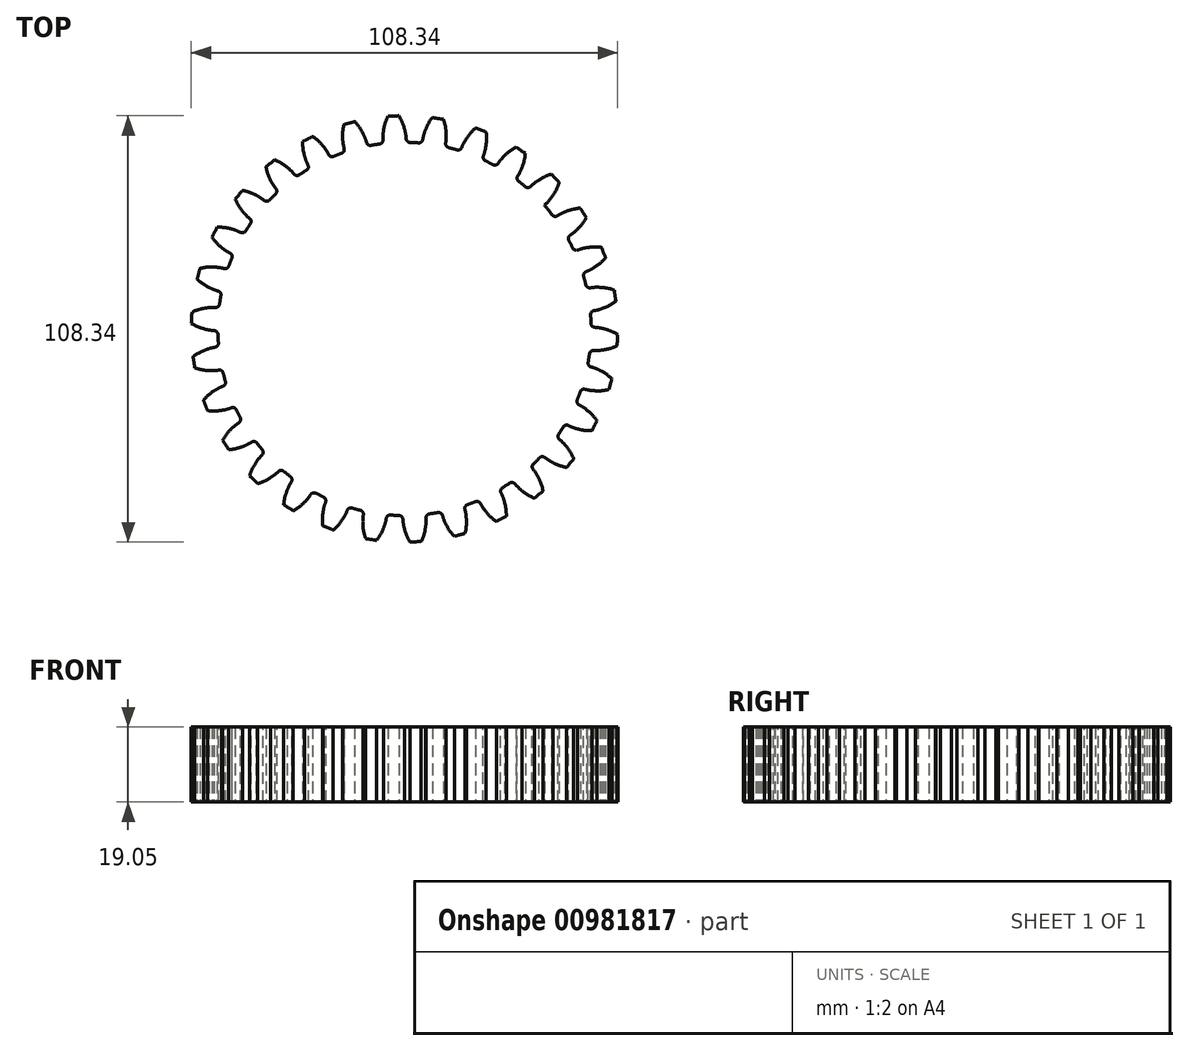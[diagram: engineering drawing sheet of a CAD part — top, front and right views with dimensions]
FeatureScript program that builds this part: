
annotation { "Feature Type Name" : "Feature", "Feature Type Description" : "" }
export const myFeature = defineFeature(function(context is Context, id is Id, definition is map)
    precondition{}
    {
        {
            var Q0;
            Q0=qCreatedBy(makeId("Top.planeOp"),FACE);
            var sketch = newSketch(context, id + "F0", { "sketchPlane" : qUnion([Q0])});
            skCircle(sketch, "E0", {"center": v(0, 0) * mm, "radius": 47.4 * mm});
            skCircle(sketch, "E1", {"center": v(0, 0) * mm, "radius": 50.8 * mm, "construction": true});
            skCircle(sketch, "E2", {"center": v(0, 0) * mm, "radius": 54.2 * mm, "construction": true});
            skLineSegment(sketch, "E3", {"start": v(0, 0) * mm, "end": v(0, 78.4) * mm, "construction": true});
            skLineSegment(sketch, "E4", {"start": v(0, 0) * mm, "end": v(-4.02, 76.64) * mm, "construction": true});
            skLineSegment(sketch, "E5", {"start": v(0, 50.8) * mm, "end": v(-70.01, 50.8) * mm, "construction": true});
            skLineSegment(sketch, "E6", {"start": v(0, 50.8) * mm, "end": v(-69.63, 32.8) * mm, "construction": true});
            skCircle(sketch, "E7", {"center": v(0, 0) * mm, "radius": 49.18 * mm, "construction": true});
            skCircle(sketch, "E8", {"center": v(0, 50.8) * mm, "radius": 12.7 * mm, "construction": true});
            skCircle(sketch, "E9", {"center": v(-12.29, 47.6) * mm, "radius": 12.7 * mm, "construction": true});
            skArc(sketch, "E10", {"start": v(0, 50.8) * mm, "mid": v(-0.57, 52.54) * mm, "end": v(-1.42, 54.17) * mm});
            skArc(sketch, "E11", {"start": v(0.4, 47.4) * mm, "mid": v(0.35, 49.12) * mm, "end": v(0, 50.8) * mm});
            skArc(sketch, "E12.MirrorCS", {"start": v(-5.36, 47.1) * mm, "mid": v(-5.48, 48.82) * mm, "end": v(-5.31, 50.52) * mm});
            skArc(sketch, "E13.MirrorCS", {"start": v(-5.31, 50.52) * mm, "mid": v(-4.92, 52.32) * mm, "end": v(-4.25, 54.02) * mm});
            skArc(sketch, "E14", {"start": v(-4.25, 54.02) * mm, "mid": v(-2.83, 54.07) * mm, "end": v(-1.42, 54.17) * mm});
            skSolve(sketch);
        }
        {
            var Q0;
            {var subQ0=sQuery(id+"F0.wireOp",EDGE,"E0");var subQ1=makeQuery(id+"F0.imprint","INTERSECT",VERTEX,{"derivedFrom":[subQ0,sQuery(id+"F0.wireOp",EDGE,"E11")]});Q0=makeQuery(id+"F0.imprint","IMPRINT",FACE,{"disambiguationData":[TD([[makeQuery(id+"F0.imprint","IMPRINT",EDGE,{"disambiguationData":[TD([[subQ1,-1.0]])],"derivedFrom":subQ0}),1.0]])]});}
            var Q1;
            Q1=makeQuery(id+"F0.imprint","IMPRINT",FACE,{"disambiguationData":[TD([[makeQuery(id+"F0.imprint","IMPRINT",EDGE,{"derivedFrom":sQuery(id+"F0.wireOp",EDGE,"E10")}),1.0]])]});
            extrude(context, id + "F1", {"entities" : qUnion([Q0, Q1]), "depth" : 19.05 * mm, "offsetDistance" : 25.4 * mm});
        }
        {
            var Q0;
            Q0=makeQuery(id+"F1.opExtrude","SWEPT_BODY",BODY,{"disambiguationData":[OSD([sQuery(id+"F0.wireOp",EDGE,"E0"),sQuery(id+"F0.wireOp",EDGE,"E10"),sQuery(id+"F0.wireOp",EDGE,"E11"),sQuery(id+"F0.wireOp",EDGE,"E12.MirrorCS"),sQuery(id+"F0.wireOp",EDGE,"E13.MirrorCS"),sQuery(id+"F0.wireOp",EDGE,"E14")])]});
            var Q1;
            Q1=makeQuery(id+"F1.opExtrude","SWEPT_FACE",FACE,{"disambiguationData":[OSD([sQuery(id+"F0.wireOp",EDGE,"E0")])]});
            circularPattern(context, id + "F2", {"entities" : qUnion([Q0]), "axis" : qUnion([Q1]), "angle" : 360 * degree, "instanceCount" : 30, "equalSpace" : true});
        }
        {
            var Q0;
            Q0=makeQuery(id+"F1.opExtrude","SWEPT_BODY",BODY,{"disambiguationData":[OSD([sQuery(id+"F0.wireOp",EDGE,"E0"),sQuery(id+"F0.wireOp",EDGE,"E10"),sQuery(id+"F0.wireOp",EDGE,"E11"),sQuery(id+"F0.wireOp",EDGE,"E12.MirrorCS"),sQuery(id+"F0.wireOp",EDGE,"E13.MirrorCS"),sQuery(id+"F0.wireOp",EDGE,"E14")])]});
            var Q1;
            Q1=makeQuery(id+"F2.opPattern","COPY",BODY,{"derivedFrom":makeQuery(id+"F1.opExtrude","SWEPT_BODY",BODY,{"disambiguationData":[OSD([sQuery(id+"F0.wireOp",EDGE,"E0"),sQuery(id+"F0.wireOp",EDGE,"E10"),sQuery(id+"F0.wireOp",EDGE,"E11"),sQuery(id+"F0.wireOp",EDGE,"E12.MirrorCS"),sQuery(id+"F0.wireOp",EDGE,"E13.MirrorCS"),sQuery(id+"F0.wireOp",EDGE,"E14")])]}),"instanceName":"1"});
            var Q2;
            Q2=makeQuery(id+"F2.opPattern","COPY",BODY,{"derivedFrom":makeQuery(id+"F1.opExtrude","SWEPT_BODY",BODY,{"disambiguationData":[OSD([sQuery(id+"F0.wireOp",EDGE,"E0"),sQuery(id+"F0.wireOp",EDGE,"E10"),sQuery(id+"F0.wireOp",EDGE,"E11"),sQuery(id+"F0.wireOp",EDGE,"E12.MirrorCS"),sQuery(id+"F0.wireOp",EDGE,"E13.MirrorCS"),sQuery(id+"F0.wireOp",EDGE,"E14")])]}),"instanceName":"2"});
            var Q3;
            Q3=makeQuery(id+"F2.opPattern","COPY",BODY,{"derivedFrom":makeQuery(id+"F1.opExtrude","SWEPT_BODY",BODY,{"disambiguationData":[OSD([sQuery(id+"F0.wireOp",EDGE,"E0"),sQuery(id+"F0.wireOp",EDGE,"E10"),sQuery(id+"F0.wireOp",EDGE,"E11"),sQuery(id+"F0.wireOp",EDGE,"E12.MirrorCS"),sQuery(id+"F0.wireOp",EDGE,"E13.MirrorCS"),sQuery(id+"F0.wireOp",EDGE,"E14")])]}),"instanceName":"4"});
            var Q4;
            Q4=makeQuery(id+"F2.opPattern","COPY",BODY,{"derivedFrom":makeQuery(id+"F1.opExtrude","SWEPT_BODY",BODY,{"disambiguationData":[OSD([sQuery(id+"F0.wireOp",EDGE,"E0"),sQuery(id+"F0.wireOp",EDGE,"E10"),sQuery(id+"F0.wireOp",EDGE,"E11"),sQuery(id+"F0.wireOp",EDGE,"E12.MirrorCS"),sQuery(id+"F0.wireOp",EDGE,"E13.MirrorCS"),sQuery(id+"F0.wireOp",EDGE,"E14")])]}),"instanceName":"3"});
            var Q5;
            Q5=makeQuery(id+"F2.opPattern","COPY",BODY,{"derivedFrom":makeQuery(id+"F1.opExtrude","SWEPT_BODY",BODY,{"disambiguationData":[OSD([sQuery(id+"F0.wireOp",EDGE,"E0"),sQuery(id+"F0.wireOp",EDGE,"E10"),sQuery(id+"F0.wireOp",EDGE,"E11"),sQuery(id+"F0.wireOp",EDGE,"E12.MirrorCS"),sQuery(id+"F0.wireOp",EDGE,"E13.MirrorCS"),sQuery(id+"F0.wireOp",EDGE,"E14")])]}),"instanceName":"6"});
            var Q6;
            Q6=makeQuery(id+"F2.opPattern","COPY",BODY,{"derivedFrom":makeQuery(id+"F1.opExtrude","SWEPT_BODY",BODY,{"disambiguationData":[OSD([sQuery(id+"F0.wireOp",EDGE,"E0"),sQuery(id+"F0.wireOp",EDGE,"E10"),sQuery(id+"F0.wireOp",EDGE,"E11"),sQuery(id+"F0.wireOp",EDGE,"E12.MirrorCS"),sQuery(id+"F0.wireOp",EDGE,"E13.MirrorCS"),sQuery(id+"F0.wireOp",EDGE,"E14")])]}),"instanceName":"5"});
            var Q7;
            Q7=makeQuery(id+"F2.opPattern","COPY",BODY,{"derivedFrom":makeQuery(id+"F1.opExtrude","SWEPT_BODY",BODY,{"disambiguationData":[OSD([sQuery(id+"F0.wireOp",EDGE,"E0"),sQuery(id+"F0.wireOp",EDGE,"E10"),sQuery(id+"F0.wireOp",EDGE,"E11"),sQuery(id+"F0.wireOp",EDGE,"E12.MirrorCS"),sQuery(id+"F0.wireOp",EDGE,"E13.MirrorCS"),sQuery(id+"F0.wireOp",EDGE,"E14")])]}),"instanceName":"7"});
            var Q8;
            Q8=makeQuery(id+"F2.opPattern","COPY",BODY,{"derivedFrom":makeQuery(id+"F1.opExtrude","SWEPT_BODY",BODY,{"disambiguationData":[OSD([sQuery(id+"F0.wireOp",EDGE,"E0"),sQuery(id+"F0.wireOp",EDGE,"E10"),sQuery(id+"F0.wireOp",EDGE,"E11"),sQuery(id+"F0.wireOp",EDGE,"E12.MirrorCS"),sQuery(id+"F0.wireOp",EDGE,"E13.MirrorCS"),sQuery(id+"F0.wireOp",EDGE,"E14")])]}),"instanceName":"8"});
            var Q9;
            Q9=makeQuery(id+"F2.opPattern","COPY",BODY,{"derivedFrom":makeQuery(id+"F1.opExtrude","SWEPT_BODY",BODY,{"disambiguationData":[OSD([sQuery(id+"F0.wireOp",EDGE,"E0"),sQuery(id+"F0.wireOp",EDGE,"E10"),sQuery(id+"F0.wireOp",EDGE,"E11"),sQuery(id+"F0.wireOp",EDGE,"E12.MirrorCS"),sQuery(id+"F0.wireOp",EDGE,"E13.MirrorCS"),sQuery(id+"F0.wireOp",EDGE,"E14")])]}),"instanceName":"9"});
            var Q10;
            Q10=makeQuery(id+"F2.opPattern","COPY",BODY,{"derivedFrom":makeQuery(id+"F1.opExtrude","SWEPT_BODY",BODY,{"disambiguationData":[OSD([sQuery(id+"F0.wireOp",EDGE,"E0"),sQuery(id+"F0.wireOp",EDGE,"E10"),sQuery(id+"F0.wireOp",EDGE,"E11"),sQuery(id+"F0.wireOp",EDGE,"E12.MirrorCS"),sQuery(id+"F0.wireOp",EDGE,"E13.MirrorCS"),sQuery(id+"F0.wireOp",EDGE,"E14")])]}),"instanceName":"10"});
            var Q11;
            Q11=makeQuery(id+"F2.opPattern","COPY",BODY,{"derivedFrom":makeQuery(id+"F1.opExtrude","SWEPT_BODY",BODY,{"disambiguationData":[OSD([sQuery(id+"F0.wireOp",EDGE,"E0"),sQuery(id+"F0.wireOp",EDGE,"E10"),sQuery(id+"F0.wireOp",EDGE,"E11"),sQuery(id+"F0.wireOp",EDGE,"E12.MirrorCS"),sQuery(id+"F0.wireOp",EDGE,"E13.MirrorCS"),sQuery(id+"F0.wireOp",EDGE,"E14")])]}),"instanceName":"11"});
            var Q12;
            Q12=makeQuery(id+"F2.opPattern","COPY",BODY,{"derivedFrom":makeQuery(id+"F1.opExtrude","SWEPT_BODY",BODY,{"disambiguationData":[OSD([sQuery(id+"F0.wireOp",EDGE,"E0"),sQuery(id+"F0.wireOp",EDGE,"E10"),sQuery(id+"F0.wireOp",EDGE,"E11"),sQuery(id+"F0.wireOp",EDGE,"E12.MirrorCS"),sQuery(id+"F0.wireOp",EDGE,"E13.MirrorCS"),sQuery(id+"F0.wireOp",EDGE,"E14")])]}),"instanceName":"12"});
            var Q13;
            Q13=makeQuery(id+"F2.opPattern","COPY",BODY,{"derivedFrom":makeQuery(id+"F1.opExtrude","SWEPT_BODY",BODY,{"disambiguationData":[OSD([sQuery(id+"F0.wireOp",EDGE,"E0"),sQuery(id+"F0.wireOp",EDGE,"E10"),sQuery(id+"F0.wireOp",EDGE,"E11"),sQuery(id+"F0.wireOp",EDGE,"E12.MirrorCS"),sQuery(id+"F0.wireOp",EDGE,"E13.MirrorCS"),sQuery(id+"F0.wireOp",EDGE,"E14")])]}),"instanceName":"13"});
            var Q14;
            Q14=makeQuery(id+"F2.opPattern","COPY",BODY,{"derivedFrom":makeQuery(id+"F1.opExtrude","SWEPT_BODY",BODY,{"disambiguationData":[OSD([sQuery(id+"F0.wireOp",EDGE,"E0"),sQuery(id+"F0.wireOp",EDGE,"E10"),sQuery(id+"F0.wireOp",EDGE,"E11"),sQuery(id+"F0.wireOp",EDGE,"E12.MirrorCS"),sQuery(id+"F0.wireOp",EDGE,"E13.MirrorCS"),sQuery(id+"F0.wireOp",EDGE,"E14")])]}),"instanceName":"14"});
            var Q15;
            Q15=makeQuery(id+"F2.opPattern","COPY",BODY,{"derivedFrom":makeQuery(id+"F1.opExtrude","SWEPT_BODY",BODY,{"disambiguationData":[OSD([sQuery(id+"F0.wireOp",EDGE,"E0"),sQuery(id+"F0.wireOp",EDGE,"E10"),sQuery(id+"F0.wireOp",EDGE,"E11"),sQuery(id+"F0.wireOp",EDGE,"E12.MirrorCS"),sQuery(id+"F0.wireOp",EDGE,"E13.MirrorCS"),sQuery(id+"F0.wireOp",EDGE,"E14")])]}),"instanceName":"16"});
            var Q16;
            Q16=makeQuery(id+"F2.opPattern","COPY",BODY,{"derivedFrom":makeQuery(id+"F1.opExtrude","SWEPT_BODY",BODY,{"disambiguationData":[OSD([sQuery(id+"F0.wireOp",EDGE,"E0"),sQuery(id+"F0.wireOp",EDGE,"E10"),sQuery(id+"F0.wireOp",EDGE,"E11"),sQuery(id+"F0.wireOp",EDGE,"E12.MirrorCS"),sQuery(id+"F0.wireOp",EDGE,"E13.MirrorCS"),sQuery(id+"F0.wireOp",EDGE,"E14")])]}),"instanceName":"17"});
            var Q17;
            Q17=makeQuery(id+"F2.opPattern","COPY",BODY,{"derivedFrom":makeQuery(id+"F1.opExtrude","SWEPT_BODY",BODY,{"disambiguationData":[OSD([sQuery(id+"F0.wireOp",EDGE,"E0"),sQuery(id+"F0.wireOp",EDGE,"E10"),sQuery(id+"F0.wireOp",EDGE,"E11"),sQuery(id+"F0.wireOp",EDGE,"E12.MirrorCS"),sQuery(id+"F0.wireOp",EDGE,"E13.MirrorCS"),sQuery(id+"F0.wireOp",EDGE,"E14")])]}),"instanceName":"15"});
            var Q18;
            Q18=makeQuery(id+"F2.opPattern","COPY",BODY,{"derivedFrom":makeQuery(id+"F1.opExtrude","SWEPT_BODY",BODY,{"disambiguationData":[OSD([sQuery(id+"F0.wireOp",EDGE,"E0"),sQuery(id+"F0.wireOp",EDGE,"E10"),sQuery(id+"F0.wireOp",EDGE,"E11"),sQuery(id+"F0.wireOp",EDGE,"E12.MirrorCS"),sQuery(id+"F0.wireOp",EDGE,"E13.MirrorCS"),sQuery(id+"F0.wireOp",EDGE,"E14")])]}),"instanceName":"18"});
            var Q19;
            Q19=makeQuery(id+"F2.opPattern","COPY",BODY,{"derivedFrom":makeQuery(id+"F1.opExtrude","SWEPT_BODY",BODY,{"disambiguationData":[OSD([sQuery(id+"F0.wireOp",EDGE,"E0"),sQuery(id+"F0.wireOp",EDGE,"E10"),sQuery(id+"F0.wireOp",EDGE,"E11"),sQuery(id+"F0.wireOp",EDGE,"E12.MirrorCS"),sQuery(id+"F0.wireOp",EDGE,"E13.MirrorCS"),sQuery(id+"F0.wireOp",EDGE,"E14")])]}),"instanceName":"19"});
            var Q20;
            Q20=makeQuery(id+"F2.opPattern","COPY",BODY,{"derivedFrom":makeQuery(id+"F1.opExtrude","SWEPT_BODY",BODY,{"disambiguationData":[OSD([sQuery(id+"F0.wireOp",EDGE,"E0"),sQuery(id+"F0.wireOp",EDGE,"E10"),sQuery(id+"F0.wireOp",EDGE,"E11"),sQuery(id+"F0.wireOp",EDGE,"E12.MirrorCS"),sQuery(id+"F0.wireOp",EDGE,"E13.MirrorCS"),sQuery(id+"F0.wireOp",EDGE,"E14")])]}),"instanceName":"20"});
            var Q21;
            Q21=makeQuery(id+"F2.opPattern","COPY",BODY,{"derivedFrom":makeQuery(id+"F1.opExtrude","SWEPT_BODY",BODY,{"disambiguationData":[OSD([sQuery(id+"F0.wireOp",EDGE,"E0"),sQuery(id+"F0.wireOp",EDGE,"E10"),sQuery(id+"F0.wireOp",EDGE,"E11"),sQuery(id+"F0.wireOp",EDGE,"E12.MirrorCS"),sQuery(id+"F0.wireOp",EDGE,"E13.MirrorCS"),sQuery(id+"F0.wireOp",EDGE,"E14")])]}),"instanceName":"21"});
            var Q22;
            Q22=makeQuery(id+"F2.opPattern","COPY",BODY,{"derivedFrom":makeQuery(id+"F1.opExtrude","SWEPT_BODY",BODY,{"disambiguationData":[OSD([sQuery(id+"F0.wireOp",EDGE,"E0"),sQuery(id+"F0.wireOp",EDGE,"E10"),sQuery(id+"F0.wireOp",EDGE,"E11"),sQuery(id+"F0.wireOp",EDGE,"E12.MirrorCS"),sQuery(id+"F0.wireOp",EDGE,"E13.MirrorCS"),sQuery(id+"F0.wireOp",EDGE,"E14")])]}),"instanceName":"22"});
            var Q23;
            Q23=makeQuery(id+"F2.opPattern","COPY",BODY,{"derivedFrom":makeQuery(id+"F1.opExtrude","SWEPT_BODY",BODY,{"disambiguationData":[OSD([sQuery(id+"F0.wireOp",EDGE,"E0"),sQuery(id+"F0.wireOp",EDGE,"E10"),sQuery(id+"F0.wireOp",EDGE,"E11"),sQuery(id+"F0.wireOp",EDGE,"E12.MirrorCS"),sQuery(id+"F0.wireOp",EDGE,"E13.MirrorCS"),sQuery(id+"F0.wireOp",EDGE,"E14")])]}),"instanceName":"23"});
            var Q24;
            Q24=makeQuery(id+"F2.opPattern","COPY",BODY,{"derivedFrom":makeQuery(id+"F1.opExtrude","SWEPT_BODY",BODY,{"disambiguationData":[OSD([sQuery(id+"F0.wireOp",EDGE,"E0"),sQuery(id+"F0.wireOp",EDGE,"E10"),sQuery(id+"F0.wireOp",EDGE,"E11"),sQuery(id+"F0.wireOp",EDGE,"E12.MirrorCS"),sQuery(id+"F0.wireOp",EDGE,"E13.MirrorCS"),sQuery(id+"F0.wireOp",EDGE,"E14")])]}),"instanceName":"24"});
            var Q25;
            Q25=makeQuery(id+"F2.opPattern","COPY",BODY,{"derivedFrom":makeQuery(id+"F1.opExtrude","SWEPT_BODY",BODY,{"disambiguationData":[OSD([sQuery(id+"F0.wireOp",EDGE,"E0"),sQuery(id+"F0.wireOp",EDGE,"E10"),sQuery(id+"F0.wireOp",EDGE,"E11"),sQuery(id+"F0.wireOp",EDGE,"E12.MirrorCS"),sQuery(id+"F0.wireOp",EDGE,"E13.MirrorCS"),sQuery(id+"F0.wireOp",EDGE,"E14")])]}),"instanceName":"25"});
            var Q26;
            Q26=makeQuery(id+"F2.opPattern","COPY",BODY,{"derivedFrom":makeQuery(id+"F1.opExtrude","SWEPT_BODY",BODY,{"disambiguationData":[OSD([sQuery(id+"F0.wireOp",EDGE,"E0"),sQuery(id+"F0.wireOp",EDGE,"E10"),sQuery(id+"F0.wireOp",EDGE,"E11"),sQuery(id+"F0.wireOp",EDGE,"E12.MirrorCS"),sQuery(id+"F0.wireOp",EDGE,"E13.MirrorCS"),sQuery(id+"F0.wireOp",EDGE,"E14")])]}),"instanceName":"26"});
            var Q27;
            Q27=makeQuery(id+"F2.opPattern","COPY",BODY,{"derivedFrom":makeQuery(id+"F1.opExtrude","SWEPT_BODY",BODY,{"disambiguationData":[OSD([sQuery(id+"F0.wireOp",EDGE,"E0"),sQuery(id+"F0.wireOp",EDGE,"E10"),sQuery(id+"F0.wireOp",EDGE,"E11"),sQuery(id+"F0.wireOp",EDGE,"E12.MirrorCS"),sQuery(id+"F0.wireOp",EDGE,"E13.MirrorCS"),sQuery(id+"F0.wireOp",EDGE,"E14")])]}),"instanceName":"27"});
            var Q28;
            Q28=makeQuery(id+"F2.opPattern","COPY",BODY,{"derivedFrom":makeQuery(id+"F1.opExtrude","SWEPT_BODY",BODY,{"disambiguationData":[OSD([sQuery(id+"F0.wireOp",EDGE,"E0"),sQuery(id+"F0.wireOp",EDGE,"E10"),sQuery(id+"F0.wireOp",EDGE,"E11"),sQuery(id+"F0.wireOp",EDGE,"E12.MirrorCS"),sQuery(id+"F0.wireOp",EDGE,"E13.MirrorCS"),sQuery(id+"F0.wireOp",EDGE,"E14")])]}),"instanceName":"28"});
            var Q29;
            Q29=makeQuery(id+"F2.opPattern","COPY",BODY,{"derivedFrom":makeQuery(id+"F1.opExtrude","SWEPT_BODY",BODY,{"disambiguationData":[OSD([sQuery(id+"F0.wireOp",EDGE,"E0"),sQuery(id+"F0.wireOp",EDGE,"E10"),sQuery(id+"F0.wireOp",EDGE,"E11"),sQuery(id+"F0.wireOp",EDGE,"E12.MirrorCS"),sQuery(id+"F0.wireOp",EDGE,"E13.MirrorCS"),sQuery(id+"F0.wireOp",EDGE,"E14")])]}),"instanceName":"29"});
            booleanBodies(context, id + "F3", {"operationType" : BooleanOperationType.UNION, "tools" : qUnion([Q0, Q1, Q2, Q3, Q4, Q5, Q6, Q7, Q8, Q9, Q10, Q11, Q12, Q13, Q14, Q15, Q16, Q17, Q18, Q19, Q20, Q21, Q22, Q23, Q24, Q25, Q26, Q27, Q28, Q29])});
        }
        {
            var Q0;
            {var subQ0=makeQuery(id+"F1.opExtrude","SWEPT_FACE",FACE,{"disambiguationData":[OSD([sQuery(id+"F0.wireOp",EDGE,"E0")])]});Q0=makeQuery(id+"F3.opBoolean","INTERSECT",EDGE,{"disambiguationData":[topologyDisambiguationEdgeConnected([makeQuery(id+"F2.opPattern","COPY",FACE,{"derivedFrom":makeQuery(id+"F1.opExtrude","SWEPT_FACE",FACE,{"disambiguationData":[OSD([sQuery(id+"F0.wireOp",EDGE,"E11")])]}),"instanceName":"21"})])],"derivedFrom":[subQ0,makeQuery(id+"F2.opPattern","COPY",FACE,{"derivedFrom":subQ0,"instanceName":"1"}),makeQuery(id+"F2.opPattern","COPY",FACE,{"derivedFrom":subQ0,"instanceName":"2"}),makeQuery(id+"F2.opPattern","COPY",FACE,{"derivedFrom":subQ0,"instanceName":"3"}),makeQuery(id+"F2.opPattern","COPY",FACE,{"derivedFrom":subQ0,"instanceName":"4"}),makeQuery(id+"F2.opPattern","COPY",FACE,{"derivedFrom":subQ0,"instanceName":"5"}),makeQuery(id+"F2.opPattern","COPY",FACE,{"derivedFrom":subQ0,"instanceName":"6"}),makeQuery(id+"F2.opPattern","COPY",FACE,{"derivedFrom":subQ0,"instanceName":"7"}),makeQuery(id+"F2.opPattern","COPY",FACE,{"derivedFrom":subQ0,"instanceName":"8"}),makeQuery(id+"F2.opPattern","COPY",FACE,{"derivedFrom":subQ0,"instanceName":"9"}),makeQuery(id+"F2.opPattern","COPY",FACE,{"derivedFrom":subQ0,"instanceName":"10"}),makeQuery(id+"F2.opPattern","COPY",FACE,{"derivedFrom":subQ0,"instanceName":"11"}),makeQuery(id+"F2.opPattern","COPY",FACE,{"derivedFrom":subQ0,"instanceName":"12"}),makeQuery(id+"F2.opPattern","COPY",FACE,{"derivedFrom":subQ0,"instanceName":"13"}),makeQuery(id+"F2.opPattern","COPY",FACE,{"derivedFrom":subQ0,"instanceName":"14"}),makeQuery(id+"F2.opPattern","COPY",FACE,{"derivedFrom":subQ0,"instanceName":"15"}),makeQuery(id+"F2.opPattern","COPY",FACE,{"derivedFrom":subQ0,"instanceName":"16"}),makeQuery(id+"F2.opPattern","COPY",FACE,{"derivedFrom":subQ0,"instanceName":"17"}),makeQuery(id+"F2.opPattern","COPY",FACE,{"derivedFrom":subQ0,"instanceName":"18"}),makeQuery(id+"F2.opPattern","COPY",FACE,{"derivedFrom":subQ0,"instanceName":"19"}),makeQuery(id+"F2.opPattern","COPY",FACE,{"derivedFrom":subQ0,"instanceName":"20"}),makeQuery(id+"F2.opPattern","COPY",FACE,{"derivedFrom":subQ0,"instanceName":"22"})]});}
            var Q1;
            {var subQ0=makeQuery(id+"F1.opExtrude","SWEPT_FACE",FACE,{"disambiguationData":[OSD([sQuery(id+"F0.wireOp",EDGE,"E0")])]});Q1=makeQuery(id+"F3.opBoolean","INTERSECT",EDGE,{"disambiguationData":[topologyDisambiguationEdgeConnected([makeQuery(id+"F2.opPattern","COPY",FACE,{"derivedFrom":makeQuery(id+"F1.opExtrude","SWEPT_FACE",FACE,{"disambiguationData":[OSD([sQuery(id+"F0.wireOp",EDGE,"E12.MirrorCS")])]}),"instanceName":"22"})])],"derivedFrom":[subQ0,makeQuery(id+"F2.opPattern","COPY",FACE,{"derivedFrom":subQ0,"instanceName":"1"}),makeQuery(id+"F2.opPattern","COPY",FACE,{"derivedFrom":subQ0,"instanceName":"2"}),makeQuery(id+"F2.opPattern","COPY",FACE,{"derivedFrom":subQ0,"instanceName":"3"}),makeQuery(id+"F2.opPattern","COPY",FACE,{"derivedFrom":subQ0,"instanceName":"4"}),makeQuery(id+"F2.opPattern","COPY",FACE,{"derivedFrom":subQ0,"instanceName":"5"}),makeQuery(id+"F2.opPattern","COPY",FACE,{"derivedFrom":subQ0,"instanceName":"6"}),makeQuery(id+"F2.opPattern","COPY",FACE,{"derivedFrom":subQ0,"instanceName":"7"}),makeQuery(id+"F2.opPattern","COPY",FACE,{"derivedFrom":subQ0,"instanceName":"8"}),makeQuery(id+"F2.opPattern","COPY",FACE,{"derivedFrom":subQ0,"instanceName":"9"}),makeQuery(id+"F2.opPattern","COPY",FACE,{"derivedFrom":subQ0,"instanceName":"10"}),makeQuery(id+"F2.opPattern","COPY",FACE,{"derivedFrom":subQ0,"instanceName":"11"}),makeQuery(id+"F2.opPattern","COPY",FACE,{"derivedFrom":subQ0,"instanceName":"12"}),makeQuery(id+"F2.opPattern","COPY",FACE,{"derivedFrom":subQ0,"instanceName":"13"}),makeQuery(id+"F2.opPattern","COPY",FACE,{"derivedFrom":subQ0,"instanceName":"14"}),makeQuery(id+"F2.opPattern","COPY",FACE,{"derivedFrom":subQ0,"instanceName":"15"}),makeQuery(id+"F2.opPattern","COPY",FACE,{"derivedFrom":subQ0,"instanceName":"16"}),makeQuery(id+"F2.opPattern","COPY",FACE,{"derivedFrom":subQ0,"instanceName":"17"}),makeQuery(id+"F2.opPattern","COPY",FACE,{"derivedFrom":subQ0,"instanceName":"18"}),makeQuery(id+"F2.opPattern","COPY",FACE,{"derivedFrom":subQ0,"instanceName":"19"}),makeQuery(id+"F2.opPattern","COPY",FACE,{"derivedFrom":subQ0,"instanceName":"20"}),makeQuery(id+"F2.opPattern","COPY",FACE,{"derivedFrom":subQ0,"instanceName":"21"}),makeQuery(id+"F2.opPattern","COPY",FACE,{"derivedFrom":subQ0,"instanceName":"23"})]});}
            var Q2;
            {var subQ0=makeQuery(id+"F1.opExtrude","SWEPT_FACE",FACE,{"disambiguationData":[OSD([sQuery(id+"F0.wireOp",EDGE,"E0")])]});Q2=makeQuery(id+"F3.opBoolean","INTERSECT",EDGE,{"disambiguationData":[topologyDisambiguationEdgeConnected([makeQuery(id+"F2.opPattern","COPY",FACE,{"derivedFrom":makeQuery(id+"F1.opExtrude","SWEPT_FACE",FACE,{"disambiguationData":[OSD([sQuery(id+"F0.wireOp",EDGE,"E11")])]}),"instanceName":"22"})])],"derivedFrom":[subQ0,makeQuery(id+"F2.opPattern","COPY",FACE,{"derivedFrom":subQ0,"instanceName":"1"}),makeQuery(id+"F2.opPattern","COPY",FACE,{"derivedFrom":subQ0,"instanceName":"2"}),makeQuery(id+"F2.opPattern","COPY",FACE,{"derivedFrom":subQ0,"instanceName":"3"}),makeQuery(id+"F2.opPattern","COPY",FACE,{"derivedFrom":subQ0,"instanceName":"4"}),makeQuery(id+"F2.opPattern","COPY",FACE,{"derivedFrom":subQ0,"instanceName":"5"}),makeQuery(id+"F2.opPattern","COPY",FACE,{"derivedFrom":subQ0,"instanceName":"6"}),makeQuery(id+"F2.opPattern","COPY",FACE,{"derivedFrom":subQ0,"instanceName":"7"}),makeQuery(id+"F2.opPattern","COPY",FACE,{"derivedFrom":subQ0,"instanceName":"8"}),makeQuery(id+"F2.opPattern","COPY",FACE,{"derivedFrom":subQ0,"instanceName":"9"}),makeQuery(id+"F2.opPattern","COPY",FACE,{"derivedFrom":subQ0,"instanceName":"10"}),makeQuery(id+"F2.opPattern","COPY",FACE,{"derivedFrom":subQ0,"instanceName":"11"}),makeQuery(id+"F2.opPattern","COPY",FACE,{"derivedFrom":subQ0,"instanceName":"12"}),makeQuery(id+"F2.opPattern","COPY",FACE,{"derivedFrom":subQ0,"instanceName":"13"}),makeQuery(id+"F2.opPattern","COPY",FACE,{"derivedFrom":subQ0,"instanceName":"14"}),makeQuery(id+"F2.opPattern","COPY",FACE,{"derivedFrom":subQ0,"instanceName":"15"}),makeQuery(id+"F2.opPattern","COPY",FACE,{"derivedFrom":subQ0,"instanceName":"16"}),makeQuery(id+"F2.opPattern","COPY",FACE,{"derivedFrom":subQ0,"instanceName":"17"}),makeQuery(id+"F2.opPattern","COPY",FACE,{"derivedFrom":subQ0,"instanceName":"18"}),makeQuery(id+"F2.opPattern","COPY",FACE,{"derivedFrom":subQ0,"instanceName":"19"}),makeQuery(id+"F2.opPattern","COPY",FACE,{"derivedFrom":subQ0,"instanceName":"20"}),makeQuery(id+"F2.opPattern","COPY",FACE,{"derivedFrom":subQ0,"instanceName":"21"}),makeQuery(id+"F2.opPattern","COPY",FACE,{"derivedFrom":subQ0,"instanceName":"23"})]});}
            var Q3;
            {var subQ0=makeQuery(id+"F1.opExtrude","SWEPT_FACE",FACE,{"disambiguationData":[OSD([sQuery(id+"F0.wireOp",EDGE,"E0")])]});Q3=makeQuery(id+"F3.opBoolean","INTERSECT",EDGE,{"disambiguationData":[topologyDisambiguationEdgeConnected([makeQuery(id+"F2.opPattern","COPY",FACE,{"derivedFrom":makeQuery(id+"F1.opExtrude","SWEPT_FACE",FACE,{"disambiguationData":[OSD([sQuery(id+"F0.wireOp",EDGE,"E12.MirrorCS")])]}),"instanceName":"23"})])],"derivedFrom":[subQ0,makeQuery(id+"F2.opPattern","COPY",FACE,{"derivedFrom":subQ0,"instanceName":"1"}),makeQuery(id+"F2.opPattern","COPY",FACE,{"derivedFrom":subQ0,"instanceName":"2"}),makeQuery(id+"F2.opPattern","COPY",FACE,{"derivedFrom":subQ0,"instanceName":"3"}),makeQuery(id+"F2.opPattern","COPY",FACE,{"derivedFrom":subQ0,"instanceName":"4"}),makeQuery(id+"F2.opPattern","COPY",FACE,{"derivedFrom":subQ0,"instanceName":"5"}),makeQuery(id+"F2.opPattern","COPY",FACE,{"derivedFrom":subQ0,"instanceName":"6"}),makeQuery(id+"F2.opPattern","COPY",FACE,{"derivedFrom":subQ0,"instanceName":"7"}),makeQuery(id+"F2.opPattern","COPY",FACE,{"derivedFrom":subQ0,"instanceName":"8"}),makeQuery(id+"F2.opPattern","COPY",FACE,{"derivedFrom":subQ0,"instanceName":"9"}),makeQuery(id+"F2.opPattern","COPY",FACE,{"derivedFrom":subQ0,"instanceName":"10"}),makeQuery(id+"F2.opPattern","COPY",FACE,{"derivedFrom":subQ0,"instanceName":"11"}),makeQuery(id+"F2.opPattern","COPY",FACE,{"derivedFrom":subQ0,"instanceName":"12"}),makeQuery(id+"F2.opPattern","COPY",FACE,{"derivedFrom":subQ0,"instanceName":"13"}),makeQuery(id+"F2.opPattern","COPY",FACE,{"derivedFrom":subQ0,"instanceName":"14"}),makeQuery(id+"F2.opPattern","COPY",FACE,{"derivedFrom":subQ0,"instanceName":"15"}),makeQuery(id+"F2.opPattern","COPY",FACE,{"derivedFrom":subQ0,"instanceName":"16"}),makeQuery(id+"F2.opPattern","COPY",FACE,{"derivedFrom":subQ0,"instanceName":"17"}),makeQuery(id+"F2.opPattern","COPY",FACE,{"derivedFrom":subQ0,"instanceName":"18"}),makeQuery(id+"F2.opPattern","COPY",FACE,{"derivedFrom":subQ0,"instanceName":"19"}),makeQuery(id+"F2.opPattern","COPY",FACE,{"derivedFrom":subQ0,"instanceName":"20"}),makeQuery(id+"F2.opPattern","COPY",FACE,{"derivedFrom":subQ0,"instanceName":"21"}),makeQuery(id+"F2.opPattern","COPY",FACE,{"derivedFrom":subQ0,"instanceName":"22"}),makeQuery(id+"F2.opPattern","COPY",FACE,{"derivedFrom":subQ0,"instanceName":"24"})]});}
            var Q4;
            {var subQ0=makeQuery(id+"F1.opExtrude","SWEPT_FACE",FACE,{"disambiguationData":[OSD([sQuery(id+"F0.wireOp",EDGE,"E0")])]});Q4=makeQuery(id+"F3.opBoolean","INTERSECT",EDGE,{"disambiguationData":[topologyDisambiguationEdgeConnected([makeQuery(id+"F2.opPattern","COPY",FACE,{"derivedFrom":makeQuery(id+"F1.opExtrude","SWEPT_FACE",FACE,{"disambiguationData":[OSD([sQuery(id+"F0.wireOp",EDGE,"E11")])]}),"instanceName":"23"})])],"derivedFrom":[subQ0,makeQuery(id+"F2.opPattern","COPY",FACE,{"derivedFrom":subQ0,"instanceName":"1"}),makeQuery(id+"F2.opPattern","COPY",FACE,{"derivedFrom":subQ0,"instanceName":"2"}),makeQuery(id+"F2.opPattern","COPY",FACE,{"derivedFrom":subQ0,"instanceName":"3"}),makeQuery(id+"F2.opPattern","COPY",FACE,{"derivedFrom":subQ0,"instanceName":"4"}),makeQuery(id+"F2.opPattern","COPY",FACE,{"derivedFrom":subQ0,"instanceName":"5"}),makeQuery(id+"F2.opPattern","COPY",FACE,{"derivedFrom":subQ0,"instanceName":"6"}),makeQuery(id+"F2.opPattern","COPY",FACE,{"derivedFrom":subQ0,"instanceName":"7"}),makeQuery(id+"F2.opPattern","COPY",FACE,{"derivedFrom":subQ0,"instanceName":"8"}),makeQuery(id+"F2.opPattern","COPY",FACE,{"derivedFrom":subQ0,"instanceName":"9"}),makeQuery(id+"F2.opPattern","COPY",FACE,{"derivedFrom":subQ0,"instanceName":"10"}),makeQuery(id+"F2.opPattern","COPY",FACE,{"derivedFrom":subQ0,"instanceName":"11"}),makeQuery(id+"F2.opPattern","COPY",FACE,{"derivedFrom":subQ0,"instanceName":"12"}),makeQuery(id+"F2.opPattern","COPY",FACE,{"derivedFrom":subQ0,"instanceName":"13"}),makeQuery(id+"F2.opPattern","COPY",FACE,{"derivedFrom":subQ0,"instanceName":"14"}),makeQuery(id+"F2.opPattern","COPY",FACE,{"derivedFrom":subQ0,"instanceName":"15"}),makeQuery(id+"F2.opPattern","COPY",FACE,{"derivedFrom":subQ0,"instanceName":"16"}),makeQuery(id+"F2.opPattern","COPY",FACE,{"derivedFrom":subQ0,"instanceName":"17"}),makeQuery(id+"F2.opPattern","COPY",FACE,{"derivedFrom":subQ0,"instanceName":"18"}),makeQuery(id+"F2.opPattern","COPY",FACE,{"derivedFrom":subQ0,"instanceName":"19"}),makeQuery(id+"F2.opPattern","COPY",FACE,{"derivedFrom":subQ0,"instanceName":"20"}),makeQuery(id+"F2.opPattern","COPY",FACE,{"derivedFrom":subQ0,"instanceName":"21"}),makeQuery(id+"F2.opPattern","COPY",FACE,{"derivedFrom":subQ0,"instanceName":"22"}),makeQuery(id+"F2.opPattern","COPY",FACE,{"derivedFrom":subQ0,"instanceName":"24"})]});}
            var Q5;
            {var subQ0=makeQuery(id+"F1.opExtrude","SWEPT_FACE",FACE,{"disambiguationData":[OSD([sQuery(id+"F0.wireOp",EDGE,"E0")])]});Q5=makeQuery(id+"F3.opBoolean","INTERSECT",EDGE,{"disambiguationData":[topologyDisambiguationEdgeConnected([makeQuery(id+"F2.opPattern","COPY",FACE,{"derivedFrom":makeQuery(id+"F1.opExtrude","SWEPT_FACE",FACE,{"disambiguationData":[OSD([sQuery(id+"F0.wireOp",EDGE,"E12.MirrorCS")])]}),"instanceName":"24"})])],"derivedFrom":[subQ0,makeQuery(id+"F2.opPattern","COPY",FACE,{"derivedFrom":subQ0,"instanceName":"1"}),makeQuery(id+"F2.opPattern","COPY",FACE,{"derivedFrom":subQ0,"instanceName":"2"}),makeQuery(id+"F2.opPattern","COPY",FACE,{"derivedFrom":subQ0,"instanceName":"3"}),makeQuery(id+"F2.opPattern","COPY",FACE,{"derivedFrom":subQ0,"instanceName":"4"}),makeQuery(id+"F2.opPattern","COPY",FACE,{"derivedFrom":subQ0,"instanceName":"5"}),makeQuery(id+"F2.opPattern","COPY",FACE,{"derivedFrom":subQ0,"instanceName":"6"}),makeQuery(id+"F2.opPattern","COPY",FACE,{"derivedFrom":subQ0,"instanceName":"7"}),makeQuery(id+"F2.opPattern","COPY",FACE,{"derivedFrom":subQ0,"instanceName":"8"}),makeQuery(id+"F2.opPattern","COPY",FACE,{"derivedFrom":subQ0,"instanceName":"9"}),makeQuery(id+"F2.opPattern","COPY",FACE,{"derivedFrom":subQ0,"instanceName":"10"}),makeQuery(id+"F2.opPattern","COPY",FACE,{"derivedFrom":subQ0,"instanceName":"11"}),makeQuery(id+"F2.opPattern","COPY",FACE,{"derivedFrom":subQ0,"instanceName":"12"}),makeQuery(id+"F2.opPattern","COPY",FACE,{"derivedFrom":subQ0,"instanceName":"13"}),makeQuery(id+"F2.opPattern","COPY",FACE,{"derivedFrom":subQ0,"instanceName":"14"}),makeQuery(id+"F2.opPattern","COPY",FACE,{"derivedFrom":subQ0,"instanceName":"15"}),makeQuery(id+"F2.opPattern","COPY",FACE,{"derivedFrom":subQ0,"instanceName":"16"}),makeQuery(id+"F2.opPattern","COPY",FACE,{"derivedFrom":subQ0,"instanceName":"17"}),makeQuery(id+"F2.opPattern","COPY",FACE,{"derivedFrom":subQ0,"instanceName":"18"}),makeQuery(id+"F2.opPattern","COPY",FACE,{"derivedFrom":subQ0,"instanceName":"19"}),makeQuery(id+"F2.opPattern","COPY",FACE,{"derivedFrom":subQ0,"instanceName":"20"}),makeQuery(id+"F2.opPattern","COPY",FACE,{"derivedFrom":subQ0,"instanceName":"21"}),makeQuery(id+"F2.opPattern","COPY",FACE,{"derivedFrom":subQ0,"instanceName":"22"}),makeQuery(id+"F2.opPattern","COPY",FACE,{"derivedFrom":subQ0,"instanceName":"23"}),makeQuery(id+"F2.opPattern","COPY",FACE,{"derivedFrom":subQ0,"instanceName":"25"})]});}
            var Q6;
            {var subQ0=makeQuery(id+"F1.opExtrude","SWEPT_FACE",FACE,{"disambiguationData":[OSD([sQuery(id+"F0.wireOp",EDGE,"E0")])]});Q6=makeQuery(id+"F3.opBoolean","INTERSECT",EDGE,{"disambiguationData":[topologyDisambiguationEdgeConnected([makeQuery(id+"F2.opPattern","COPY",FACE,{"derivedFrom":makeQuery(id+"F1.opExtrude","SWEPT_FACE",FACE,{"disambiguationData":[OSD([sQuery(id+"F0.wireOp",EDGE,"E11")])]}),"instanceName":"24"})])],"derivedFrom":[subQ0,makeQuery(id+"F2.opPattern","COPY",FACE,{"derivedFrom":subQ0,"instanceName":"1"}),makeQuery(id+"F2.opPattern","COPY",FACE,{"derivedFrom":subQ0,"instanceName":"2"}),makeQuery(id+"F2.opPattern","COPY",FACE,{"derivedFrom":subQ0,"instanceName":"3"}),makeQuery(id+"F2.opPattern","COPY",FACE,{"derivedFrom":subQ0,"instanceName":"4"}),makeQuery(id+"F2.opPattern","COPY",FACE,{"derivedFrom":subQ0,"instanceName":"5"}),makeQuery(id+"F2.opPattern","COPY",FACE,{"derivedFrom":subQ0,"instanceName":"6"}),makeQuery(id+"F2.opPattern","COPY",FACE,{"derivedFrom":subQ0,"instanceName":"7"}),makeQuery(id+"F2.opPattern","COPY",FACE,{"derivedFrom":subQ0,"instanceName":"8"}),makeQuery(id+"F2.opPattern","COPY",FACE,{"derivedFrom":subQ0,"instanceName":"9"}),makeQuery(id+"F2.opPattern","COPY",FACE,{"derivedFrom":subQ0,"instanceName":"10"}),makeQuery(id+"F2.opPattern","COPY",FACE,{"derivedFrom":subQ0,"instanceName":"11"}),makeQuery(id+"F2.opPattern","COPY",FACE,{"derivedFrom":subQ0,"instanceName":"12"}),makeQuery(id+"F2.opPattern","COPY",FACE,{"derivedFrom":subQ0,"instanceName":"13"}),makeQuery(id+"F2.opPattern","COPY",FACE,{"derivedFrom":subQ0,"instanceName":"14"}),makeQuery(id+"F2.opPattern","COPY",FACE,{"derivedFrom":subQ0,"instanceName":"15"}),makeQuery(id+"F2.opPattern","COPY",FACE,{"derivedFrom":subQ0,"instanceName":"16"}),makeQuery(id+"F2.opPattern","COPY",FACE,{"derivedFrom":subQ0,"instanceName":"17"}),makeQuery(id+"F2.opPattern","COPY",FACE,{"derivedFrom":subQ0,"instanceName":"18"}),makeQuery(id+"F2.opPattern","COPY",FACE,{"derivedFrom":subQ0,"instanceName":"19"}),makeQuery(id+"F2.opPattern","COPY",FACE,{"derivedFrom":subQ0,"instanceName":"20"}),makeQuery(id+"F2.opPattern","COPY",FACE,{"derivedFrom":subQ0,"instanceName":"21"}),makeQuery(id+"F2.opPattern","COPY",FACE,{"derivedFrom":subQ0,"instanceName":"22"}),makeQuery(id+"F2.opPattern","COPY",FACE,{"derivedFrom":subQ0,"instanceName":"23"}),makeQuery(id+"F2.opPattern","COPY",FACE,{"derivedFrom":subQ0,"instanceName":"25"})]});}
            var Q7;
            {var subQ0=makeQuery(id+"F1.opExtrude","SWEPT_FACE",FACE,{"disambiguationData":[OSD([sQuery(id+"F0.wireOp",EDGE,"E0")])]});Q7=makeQuery(id+"F3.opBoolean","INTERSECT",EDGE,{"disambiguationData":[topologyDisambiguationEdgeConnected([makeQuery(id+"F2.opPattern","COPY",FACE,{"derivedFrom":makeQuery(id+"F1.opExtrude","SWEPT_FACE",FACE,{"disambiguationData":[OSD([sQuery(id+"F0.wireOp",EDGE,"E12.MirrorCS")])]}),"instanceName":"25"})])],"derivedFrom":[subQ0,makeQuery(id+"F2.opPattern","COPY",FACE,{"derivedFrom":subQ0,"instanceName":"1"}),makeQuery(id+"F2.opPattern","COPY",FACE,{"derivedFrom":subQ0,"instanceName":"2"}),makeQuery(id+"F2.opPattern","COPY",FACE,{"derivedFrom":subQ0,"instanceName":"3"}),makeQuery(id+"F2.opPattern","COPY",FACE,{"derivedFrom":subQ0,"instanceName":"4"}),makeQuery(id+"F2.opPattern","COPY",FACE,{"derivedFrom":subQ0,"instanceName":"5"}),makeQuery(id+"F2.opPattern","COPY",FACE,{"derivedFrom":subQ0,"instanceName":"6"}),makeQuery(id+"F2.opPattern","COPY",FACE,{"derivedFrom":subQ0,"instanceName":"7"}),makeQuery(id+"F2.opPattern","COPY",FACE,{"derivedFrom":subQ0,"instanceName":"8"}),makeQuery(id+"F2.opPattern","COPY",FACE,{"derivedFrom":subQ0,"instanceName":"9"}),makeQuery(id+"F2.opPattern","COPY",FACE,{"derivedFrom":subQ0,"instanceName":"10"}),makeQuery(id+"F2.opPattern","COPY",FACE,{"derivedFrom":subQ0,"instanceName":"11"}),makeQuery(id+"F2.opPattern","COPY",FACE,{"derivedFrom":subQ0,"instanceName":"12"}),makeQuery(id+"F2.opPattern","COPY",FACE,{"derivedFrom":subQ0,"instanceName":"13"}),makeQuery(id+"F2.opPattern","COPY",FACE,{"derivedFrom":subQ0,"instanceName":"14"}),makeQuery(id+"F2.opPattern","COPY",FACE,{"derivedFrom":subQ0,"instanceName":"15"}),makeQuery(id+"F2.opPattern","COPY",FACE,{"derivedFrom":subQ0,"instanceName":"16"}),makeQuery(id+"F2.opPattern","COPY",FACE,{"derivedFrom":subQ0,"instanceName":"17"}),makeQuery(id+"F2.opPattern","COPY",FACE,{"derivedFrom":subQ0,"instanceName":"18"}),makeQuery(id+"F2.opPattern","COPY",FACE,{"derivedFrom":subQ0,"instanceName":"19"}),makeQuery(id+"F2.opPattern","COPY",FACE,{"derivedFrom":subQ0,"instanceName":"20"}),makeQuery(id+"F2.opPattern","COPY",FACE,{"derivedFrom":subQ0,"instanceName":"21"}),makeQuery(id+"F2.opPattern","COPY",FACE,{"derivedFrom":subQ0,"instanceName":"22"}),makeQuery(id+"F2.opPattern","COPY",FACE,{"derivedFrom":subQ0,"instanceName":"23"}),makeQuery(id+"F2.opPattern","COPY",FACE,{"derivedFrom":subQ0,"instanceName":"24"}),makeQuery(id+"F2.opPattern","COPY",FACE,{"derivedFrom":subQ0,"instanceName":"26"})]});}
            var Q8;
            {var subQ0=makeQuery(id+"F1.opExtrude","SWEPT_FACE",FACE,{"disambiguationData":[OSD([sQuery(id+"F0.wireOp",EDGE,"E0")])]});Q8=makeQuery(id+"F3.opBoolean","INTERSECT",EDGE,{"disambiguationData":[topologyDisambiguationEdgeConnected([makeQuery(id+"F2.opPattern","COPY",FACE,{"derivedFrom":makeQuery(id+"F1.opExtrude","SWEPT_FACE",FACE,{"disambiguationData":[OSD([sQuery(id+"F0.wireOp",EDGE,"E11")])]}),"instanceName":"25"})])],"derivedFrom":[subQ0,makeQuery(id+"F2.opPattern","COPY",FACE,{"derivedFrom":subQ0,"instanceName":"1"}),makeQuery(id+"F2.opPattern","COPY",FACE,{"derivedFrom":subQ0,"instanceName":"2"}),makeQuery(id+"F2.opPattern","COPY",FACE,{"derivedFrom":subQ0,"instanceName":"3"}),makeQuery(id+"F2.opPattern","COPY",FACE,{"derivedFrom":subQ0,"instanceName":"4"}),makeQuery(id+"F2.opPattern","COPY",FACE,{"derivedFrom":subQ0,"instanceName":"5"}),makeQuery(id+"F2.opPattern","COPY",FACE,{"derivedFrom":subQ0,"instanceName":"6"}),makeQuery(id+"F2.opPattern","COPY",FACE,{"derivedFrom":subQ0,"instanceName":"7"}),makeQuery(id+"F2.opPattern","COPY",FACE,{"derivedFrom":subQ0,"instanceName":"8"}),makeQuery(id+"F2.opPattern","COPY",FACE,{"derivedFrom":subQ0,"instanceName":"9"}),makeQuery(id+"F2.opPattern","COPY",FACE,{"derivedFrom":subQ0,"instanceName":"10"}),makeQuery(id+"F2.opPattern","COPY",FACE,{"derivedFrom":subQ0,"instanceName":"11"}),makeQuery(id+"F2.opPattern","COPY",FACE,{"derivedFrom":subQ0,"instanceName":"12"}),makeQuery(id+"F2.opPattern","COPY",FACE,{"derivedFrom":subQ0,"instanceName":"13"}),makeQuery(id+"F2.opPattern","COPY",FACE,{"derivedFrom":subQ0,"instanceName":"14"}),makeQuery(id+"F2.opPattern","COPY",FACE,{"derivedFrom":subQ0,"instanceName":"15"}),makeQuery(id+"F2.opPattern","COPY",FACE,{"derivedFrom":subQ0,"instanceName":"16"}),makeQuery(id+"F2.opPattern","COPY",FACE,{"derivedFrom":subQ0,"instanceName":"17"}),makeQuery(id+"F2.opPattern","COPY",FACE,{"derivedFrom":subQ0,"instanceName":"18"}),makeQuery(id+"F2.opPattern","COPY",FACE,{"derivedFrom":subQ0,"instanceName":"19"}),makeQuery(id+"F2.opPattern","COPY",FACE,{"derivedFrom":subQ0,"instanceName":"20"}),makeQuery(id+"F2.opPattern","COPY",FACE,{"derivedFrom":subQ0,"instanceName":"21"}),makeQuery(id+"F2.opPattern","COPY",FACE,{"derivedFrom":subQ0,"instanceName":"22"}),makeQuery(id+"F2.opPattern","COPY",FACE,{"derivedFrom":subQ0,"instanceName":"23"}),makeQuery(id+"F2.opPattern","COPY",FACE,{"derivedFrom":subQ0,"instanceName":"24"}),makeQuery(id+"F2.opPattern","COPY",FACE,{"derivedFrom":subQ0,"instanceName":"26"})]});}
            var Q9;
            {var subQ0=makeQuery(id+"F1.opExtrude","SWEPT_FACE",FACE,{"disambiguationData":[OSD([sQuery(id+"F0.wireOp",EDGE,"E0")])]});Q9=makeQuery(id+"F3.opBoolean","INTERSECT",EDGE,{"disambiguationData":[topologyDisambiguationEdgeConnected([makeQuery(id+"F2.opPattern","COPY",FACE,{"derivedFrom":makeQuery(id+"F1.opExtrude","SWEPT_FACE",FACE,{"disambiguationData":[OSD([sQuery(id+"F0.wireOp",EDGE,"E11")])]}),"instanceName":"26"})])],"derivedFrom":[subQ0,makeQuery(id+"F2.opPattern","COPY",FACE,{"derivedFrom":subQ0,"instanceName":"1"}),makeQuery(id+"F2.opPattern","COPY",FACE,{"derivedFrom":subQ0,"instanceName":"2"}),makeQuery(id+"F2.opPattern","COPY",FACE,{"derivedFrom":subQ0,"instanceName":"3"}),makeQuery(id+"F2.opPattern","COPY",FACE,{"derivedFrom":subQ0,"instanceName":"4"}),makeQuery(id+"F2.opPattern","COPY",FACE,{"derivedFrom":subQ0,"instanceName":"5"}),makeQuery(id+"F2.opPattern","COPY",FACE,{"derivedFrom":subQ0,"instanceName":"6"}),makeQuery(id+"F2.opPattern","COPY",FACE,{"derivedFrom":subQ0,"instanceName":"7"}),makeQuery(id+"F2.opPattern","COPY",FACE,{"derivedFrom":subQ0,"instanceName":"8"}),makeQuery(id+"F2.opPattern","COPY",FACE,{"derivedFrom":subQ0,"instanceName":"9"}),makeQuery(id+"F2.opPattern","COPY",FACE,{"derivedFrom":subQ0,"instanceName":"10"}),makeQuery(id+"F2.opPattern","COPY",FACE,{"derivedFrom":subQ0,"instanceName":"11"}),makeQuery(id+"F2.opPattern","COPY",FACE,{"derivedFrom":subQ0,"instanceName":"12"}),makeQuery(id+"F2.opPattern","COPY",FACE,{"derivedFrom":subQ0,"instanceName":"13"}),makeQuery(id+"F2.opPattern","COPY",FACE,{"derivedFrom":subQ0,"instanceName":"14"}),makeQuery(id+"F2.opPattern","COPY",FACE,{"derivedFrom":subQ0,"instanceName":"15"}),makeQuery(id+"F2.opPattern","COPY",FACE,{"derivedFrom":subQ0,"instanceName":"16"}),makeQuery(id+"F2.opPattern","COPY",FACE,{"derivedFrom":subQ0,"instanceName":"17"}),makeQuery(id+"F2.opPattern","COPY",FACE,{"derivedFrom":subQ0,"instanceName":"18"}),makeQuery(id+"F2.opPattern","COPY",FACE,{"derivedFrom":subQ0,"instanceName":"19"}),makeQuery(id+"F2.opPattern","COPY",FACE,{"derivedFrom":subQ0,"instanceName":"20"}),makeQuery(id+"F2.opPattern","COPY",FACE,{"derivedFrom":subQ0,"instanceName":"21"}),makeQuery(id+"F2.opPattern","COPY",FACE,{"derivedFrom":subQ0,"instanceName":"22"}),makeQuery(id+"F2.opPattern","COPY",FACE,{"derivedFrom":subQ0,"instanceName":"23"}),makeQuery(id+"F2.opPattern","COPY",FACE,{"derivedFrom":subQ0,"instanceName":"24"}),makeQuery(id+"F2.opPattern","COPY",FACE,{"derivedFrom":subQ0,"instanceName":"25"}),makeQuery(id+"F2.opPattern","COPY",FACE,{"derivedFrom":subQ0,"instanceName":"27"})]});}
            var Q10;
            {var subQ0=makeQuery(id+"F1.opExtrude","SWEPT_FACE",FACE,{"disambiguationData":[OSD([sQuery(id+"F0.wireOp",EDGE,"E0")])]});Q10=makeQuery(id+"F3.opBoolean","INTERSECT",EDGE,{"disambiguationData":[topologyDisambiguationEdgeConnected([makeQuery(id+"F2.opPattern","COPY",FACE,{"derivedFrom":makeQuery(id+"F1.opExtrude","SWEPT_FACE",FACE,{"disambiguationData":[OSD([sQuery(id+"F0.wireOp",EDGE,"E12.MirrorCS")])]}),"instanceName":"26"})])],"derivedFrom":[subQ0,makeQuery(id+"F2.opPattern","COPY",FACE,{"derivedFrom":subQ0,"instanceName":"1"}),makeQuery(id+"F2.opPattern","COPY",FACE,{"derivedFrom":subQ0,"instanceName":"2"}),makeQuery(id+"F2.opPattern","COPY",FACE,{"derivedFrom":subQ0,"instanceName":"3"}),makeQuery(id+"F2.opPattern","COPY",FACE,{"derivedFrom":subQ0,"instanceName":"4"}),makeQuery(id+"F2.opPattern","COPY",FACE,{"derivedFrom":subQ0,"instanceName":"5"}),makeQuery(id+"F2.opPattern","COPY",FACE,{"derivedFrom":subQ0,"instanceName":"6"}),makeQuery(id+"F2.opPattern","COPY",FACE,{"derivedFrom":subQ0,"instanceName":"7"}),makeQuery(id+"F2.opPattern","COPY",FACE,{"derivedFrom":subQ0,"instanceName":"8"}),makeQuery(id+"F2.opPattern","COPY",FACE,{"derivedFrom":subQ0,"instanceName":"9"}),makeQuery(id+"F2.opPattern","COPY",FACE,{"derivedFrom":subQ0,"instanceName":"10"}),makeQuery(id+"F2.opPattern","COPY",FACE,{"derivedFrom":subQ0,"instanceName":"11"}),makeQuery(id+"F2.opPattern","COPY",FACE,{"derivedFrom":subQ0,"instanceName":"12"}),makeQuery(id+"F2.opPattern","COPY",FACE,{"derivedFrom":subQ0,"instanceName":"13"}),makeQuery(id+"F2.opPattern","COPY",FACE,{"derivedFrom":subQ0,"instanceName":"14"}),makeQuery(id+"F2.opPattern","COPY",FACE,{"derivedFrom":subQ0,"instanceName":"15"}),makeQuery(id+"F2.opPattern","COPY",FACE,{"derivedFrom":subQ0,"instanceName":"16"}),makeQuery(id+"F2.opPattern","COPY",FACE,{"derivedFrom":subQ0,"instanceName":"17"}),makeQuery(id+"F2.opPattern","COPY",FACE,{"derivedFrom":subQ0,"instanceName":"18"}),makeQuery(id+"F2.opPattern","COPY",FACE,{"derivedFrom":subQ0,"instanceName":"19"}),makeQuery(id+"F2.opPattern","COPY",FACE,{"derivedFrom":subQ0,"instanceName":"20"}),makeQuery(id+"F2.opPattern","COPY",FACE,{"derivedFrom":subQ0,"instanceName":"21"}),makeQuery(id+"F2.opPattern","COPY",FACE,{"derivedFrom":subQ0,"instanceName":"22"}),makeQuery(id+"F2.opPattern","COPY",FACE,{"derivedFrom":subQ0,"instanceName":"23"}),makeQuery(id+"F2.opPattern","COPY",FACE,{"derivedFrom":subQ0,"instanceName":"24"}),makeQuery(id+"F2.opPattern","COPY",FACE,{"derivedFrom":subQ0,"instanceName":"25"}),makeQuery(id+"F2.opPattern","COPY",FACE,{"derivedFrom":subQ0,"instanceName":"27"})]});}
            var Q11;
            {var subQ0=makeQuery(id+"F1.opExtrude","SWEPT_FACE",FACE,{"disambiguationData":[OSD([sQuery(id+"F0.wireOp",EDGE,"E0")])]});Q11=makeQuery(id+"F3.opBoolean","INTERSECT",EDGE,{"disambiguationData":[topologyDisambiguationEdgeConnected([makeQuery(id+"F2.opPattern","COPY",FACE,{"derivedFrom":makeQuery(id+"F1.opExtrude","SWEPT_FACE",FACE,{"disambiguationData":[OSD([sQuery(id+"F0.wireOp",EDGE,"E12.MirrorCS")])]}),"instanceName":"27"})])],"derivedFrom":[subQ0,makeQuery(id+"F2.opPattern","COPY",FACE,{"derivedFrom":subQ0,"instanceName":"1"}),makeQuery(id+"F2.opPattern","COPY",FACE,{"derivedFrom":subQ0,"instanceName":"2"}),makeQuery(id+"F2.opPattern","COPY",FACE,{"derivedFrom":subQ0,"instanceName":"3"}),makeQuery(id+"F2.opPattern","COPY",FACE,{"derivedFrom":subQ0,"instanceName":"4"}),makeQuery(id+"F2.opPattern","COPY",FACE,{"derivedFrom":subQ0,"instanceName":"5"}),makeQuery(id+"F2.opPattern","COPY",FACE,{"derivedFrom":subQ0,"instanceName":"6"}),makeQuery(id+"F2.opPattern","COPY",FACE,{"derivedFrom":subQ0,"instanceName":"7"}),makeQuery(id+"F2.opPattern","COPY",FACE,{"derivedFrom":subQ0,"instanceName":"8"}),makeQuery(id+"F2.opPattern","COPY",FACE,{"derivedFrom":subQ0,"instanceName":"9"}),makeQuery(id+"F2.opPattern","COPY",FACE,{"derivedFrom":subQ0,"instanceName":"10"}),makeQuery(id+"F2.opPattern","COPY",FACE,{"derivedFrom":subQ0,"instanceName":"11"}),makeQuery(id+"F2.opPattern","COPY",FACE,{"derivedFrom":subQ0,"instanceName":"12"}),makeQuery(id+"F2.opPattern","COPY",FACE,{"derivedFrom":subQ0,"instanceName":"13"}),makeQuery(id+"F2.opPattern","COPY",FACE,{"derivedFrom":subQ0,"instanceName":"14"}),makeQuery(id+"F2.opPattern","COPY",FACE,{"derivedFrom":subQ0,"instanceName":"15"}),makeQuery(id+"F2.opPattern","COPY",FACE,{"derivedFrom":subQ0,"instanceName":"16"}),makeQuery(id+"F2.opPattern","COPY",FACE,{"derivedFrom":subQ0,"instanceName":"17"}),makeQuery(id+"F2.opPattern","COPY",FACE,{"derivedFrom":subQ0,"instanceName":"18"}),makeQuery(id+"F2.opPattern","COPY",FACE,{"derivedFrom":subQ0,"instanceName":"19"}),makeQuery(id+"F2.opPattern","COPY",FACE,{"derivedFrom":subQ0,"instanceName":"20"}),makeQuery(id+"F2.opPattern","COPY",FACE,{"derivedFrom":subQ0,"instanceName":"21"}),makeQuery(id+"F2.opPattern","COPY",FACE,{"derivedFrom":subQ0,"instanceName":"22"}),makeQuery(id+"F2.opPattern","COPY",FACE,{"derivedFrom":subQ0,"instanceName":"23"}),makeQuery(id+"F2.opPattern","COPY",FACE,{"derivedFrom":subQ0,"instanceName":"24"}),makeQuery(id+"F2.opPattern","COPY",FACE,{"derivedFrom":subQ0,"instanceName":"25"}),makeQuery(id+"F2.opPattern","COPY",FACE,{"derivedFrom":subQ0,"instanceName":"26"}),makeQuery(id+"F2.opPattern","COPY",FACE,{"derivedFrom":subQ0,"instanceName":"28"})]});}
            var Q12;
            {var subQ0=makeQuery(id+"F1.opExtrude","SWEPT_FACE",FACE,{"disambiguationData":[OSD([sQuery(id+"F0.wireOp",EDGE,"E0")])]});Q12=makeQuery(id+"F3.opBoolean","INTERSECT",EDGE,{"disambiguationData":[topologyDisambiguationEdgeConnected([makeQuery(id+"F2.opPattern","COPY",FACE,{"derivedFrom":makeQuery(id+"F1.opExtrude","SWEPT_FACE",FACE,{"disambiguationData":[OSD([sQuery(id+"F0.wireOp",EDGE,"E12.MirrorCS")])]}),"instanceName":"28"})])],"derivedFrom":[subQ0,makeQuery(id+"F2.opPattern","COPY",FACE,{"derivedFrom":subQ0,"instanceName":"1"}),makeQuery(id+"F2.opPattern","COPY",FACE,{"derivedFrom":subQ0,"instanceName":"2"}),makeQuery(id+"F2.opPattern","COPY",FACE,{"derivedFrom":subQ0,"instanceName":"3"}),makeQuery(id+"F2.opPattern","COPY",FACE,{"derivedFrom":subQ0,"instanceName":"4"}),makeQuery(id+"F2.opPattern","COPY",FACE,{"derivedFrom":subQ0,"instanceName":"5"}),makeQuery(id+"F2.opPattern","COPY",FACE,{"derivedFrom":subQ0,"instanceName":"6"}),makeQuery(id+"F2.opPattern","COPY",FACE,{"derivedFrom":subQ0,"instanceName":"7"}),makeQuery(id+"F2.opPattern","COPY",FACE,{"derivedFrom":subQ0,"instanceName":"8"}),makeQuery(id+"F2.opPattern","COPY",FACE,{"derivedFrom":subQ0,"instanceName":"9"}),makeQuery(id+"F2.opPattern","COPY",FACE,{"derivedFrom":subQ0,"instanceName":"10"}),makeQuery(id+"F2.opPattern","COPY",FACE,{"derivedFrom":subQ0,"instanceName":"11"}),makeQuery(id+"F2.opPattern","COPY",FACE,{"derivedFrom":subQ0,"instanceName":"12"}),makeQuery(id+"F2.opPattern","COPY",FACE,{"derivedFrom":subQ0,"instanceName":"13"}),makeQuery(id+"F2.opPattern","COPY",FACE,{"derivedFrom":subQ0,"instanceName":"14"}),makeQuery(id+"F2.opPattern","COPY",FACE,{"derivedFrom":subQ0,"instanceName":"15"}),makeQuery(id+"F2.opPattern","COPY",FACE,{"derivedFrom":subQ0,"instanceName":"16"}),makeQuery(id+"F2.opPattern","COPY",FACE,{"derivedFrom":subQ0,"instanceName":"17"}),makeQuery(id+"F2.opPattern","COPY",FACE,{"derivedFrom":subQ0,"instanceName":"18"}),makeQuery(id+"F2.opPattern","COPY",FACE,{"derivedFrom":subQ0,"instanceName":"19"}),makeQuery(id+"F2.opPattern","COPY",FACE,{"derivedFrom":subQ0,"instanceName":"20"}),makeQuery(id+"F2.opPattern","COPY",FACE,{"derivedFrom":subQ0,"instanceName":"21"}),makeQuery(id+"F2.opPattern","COPY",FACE,{"derivedFrom":subQ0,"instanceName":"22"}),makeQuery(id+"F2.opPattern","COPY",FACE,{"derivedFrom":subQ0,"instanceName":"23"}),makeQuery(id+"F2.opPattern","COPY",FACE,{"derivedFrom":subQ0,"instanceName":"24"}),makeQuery(id+"F2.opPattern","COPY",FACE,{"derivedFrom":subQ0,"instanceName":"25"}),makeQuery(id+"F2.opPattern","COPY",FACE,{"derivedFrom":subQ0,"instanceName":"26"}),makeQuery(id+"F2.opPattern","COPY",FACE,{"derivedFrom":subQ0,"instanceName":"27"}),makeQuery(id+"F2.opPattern","COPY",FACE,{"derivedFrom":subQ0,"instanceName":"29"})]});}
            var Q13;
            {var subQ0=makeQuery(id+"F1.opExtrude","SWEPT_FACE",FACE,{"disambiguationData":[OSD([sQuery(id+"F0.wireOp",EDGE,"E0")])]});Q13=makeQuery(id+"F3.opBoolean","INTERSECT",EDGE,{"disambiguationData":[topologyDisambiguationEdgeConnected([makeQuery(id+"F2.opPattern","COPY",FACE,{"derivedFrom":makeQuery(id+"F1.opExtrude","SWEPT_FACE",FACE,{"disambiguationData":[OSD([sQuery(id+"F0.wireOp",EDGE,"E12.MirrorCS")])]}),"instanceName":"29"})])],"derivedFrom":[subQ0,makeQuery(id+"F2.opPattern","COPY",FACE,{"derivedFrom":subQ0,"instanceName":"1"}),makeQuery(id+"F2.opPattern","COPY",FACE,{"derivedFrom":subQ0,"instanceName":"2"}),makeQuery(id+"F2.opPattern","COPY",FACE,{"derivedFrom":subQ0,"instanceName":"3"}),makeQuery(id+"F2.opPattern","COPY",FACE,{"derivedFrom":subQ0,"instanceName":"4"}),makeQuery(id+"F2.opPattern","COPY",FACE,{"derivedFrom":subQ0,"instanceName":"5"}),makeQuery(id+"F2.opPattern","COPY",FACE,{"derivedFrom":subQ0,"instanceName":"6"}),makeQuery(id+"F2.opPattern","COPY",FACE,{"derivedFrom":subQ0,"instanceName":"7"}),makeQuery(id+"F2.opPattern","COPY",FACE,{"derivedFrom":subQ0,"instanceName":"8"}),makeQuery(id+"F2.opPattern","COPY",FACE,{"derivedFrom":subQ0,"instanceName":"9"}),makeQuery(id+"F2.opPattern","COPY",FACE,{"derivedFrom":subQ0,"instanceName":"10"}),makeQuery(id+"F2.opPattern","COPY",FACE,{"derivedFrom":subQ0,"instanceName":"11"}),makeQuery(id+"F2.opPattern","COPY",FACE,{"derivedFrom":subQ0,"instanceName":"12"}),makeQuery(id+"F2.opPattern","COPY",FACE,{"derivedFrom":subQ0,"instanceName":"13"}),makeQuery(id+"F2.opPattern","COPY",FACE,{"derivedFrom":subQ0,"instanceName":"14"}),makeQuery(id+"F2.opPattern","COPY",FACE,{"derivedFrom":subQ0,"instanceName":"15"}),makeQuery(id+"F2.opPattern","COPY",FACE,{"derivedFrom":subQ0,"instanceName":"16"}),makeQuery(id+"F2.opPattern","COPY",FACE,{"derivedFrom":subQ0,"instanceName":"17"}),makeQuery(id+"F2.opPattern","COPY",FACE,{"derivedFrom":subQ0,"instanceName":"18"}),makeQuery(id+"F2.opPattern","COPY",FACE,{"derivedFrom":subQ0,"instanceName":"19"}),makeQuery(id+"F2.opPattern","COPY",FACE,{"derivedFrom":subQ0,"instanceName":"20"}),makeQuery(id+"F2.opPattern","COPY",FACE,{"derivedFrom":subQ0,"instanceName":"21"}),makeQuery(id+"F2.opPattern","COPY",FACE,{"derivedFrom":subQ0,"instanceName":"22"}),makeQuery(id+"F2.opPattern","COPY",FACE,{"derivedFrom":subQ0,"instanceName":"23"}),makeQuery(id+"F2.opPattern","COPY",FACE,{"derivedFrom":subQ0,"instanceName":"24"}),makeQuery(id+"F2.opPattern","COPY",FACE,{"derivedFrom":subQ0,"instanceName":"25"}),makeQuery(id+"F2.opPattern","COPY",FACE,{"derivedFrom":subQ0,"instanceName":"26"}),makeQuery(id+"F2.opPattern","COPY",FACE,{"derivedFrom":subQ0,"instanceName":"27"}),makeQuery(id+"F2.opPattern","COPY",FACE,{"derivedFrom":subQ0,"instanceName":"28"})]});}
            var Q14;
            Q14=makeQuery(id+"F1.opExtrude","SWEPT_EDGE",EDGE,{"disambiguationData":[OSD([sQuery(id+"F0.wireOp",EDGE,"E0"),sQuery(id+"F0.wireOp",EDGE,"E12.MirrorCS")])]});
            var Q15;
            {var subQ0=makeQuery(id+"F1.opExtrude","SWEPT_FACE",FACE,{"disambiguationData":[OSD([sQuery(id+"F0.wireOp",EDGE,"E0")])]});Q15=makeQuery(id+"F3.opBoolean","INTERSECT",EDGE,{"disambiguationData":[topologyDisambiguationEdgeConnected([makeQuery(id+"F2.opPattern","COPY",FACE,{"derivedFrom":makeQuery(id+"F1.opExtrude","SWEPT_FACE",FACE,{"disambiguationData":[OSD([sQuery(id+"F0.wireOp",EDGE,"E12.MirrorCS")])]}),"instanceName":"1"})])],"derivedFrom":[subQ0,makeQuery(id+"F2.opPattern","COPY",FACE,{"derivedFrom":subQ0,"instanceName":"2"})]});}
            var Q16;
            {var subQ0=makeQuery(id+"F1.opExtrude","SWEPT_FACE",FACE,{"disambiguationData":[OSD([sQuery(id+"F0.wireOp",EDGE,"E0")])]});Q16=makeQuery(id+"F3.opBoolean","INTERSECT",EDGE,{"disambiguationData":[topologyDisambiguationEdgeConnected([makeQuery(id+"F2.opPattern","COPY",FACE,{"derivedFrom":makeQuery(id+"F1.opExtrude","SWEPT_FACE",FACE,{"disambiguationData":[OSD([sQuery(id+"F0.wireOp",EDGE,"E12.MirrorCS")])]}),"instanceName":"2"})])],"derivedFrom":[subQ0,makeQuery(id+"F2.opPattern","COPY",FACE,{"derivedFrom":subQ0,"instanceName":"1"}),makeQuery(id+"F2.opPattern","COPY",FACE,{"derivedFrom":subQ0,"instanceName":"4"})]});}
            var Q17;
            {var subQ0=makeQuery(id+"F1.opExtrude","SWEPT_FACE",FACE,{"disambiguationData":[OSD([sQuery(id+"F0.wireOp",EDGE,"E0")])]});Q17=makeQuery(id+"F3.opBoolean","INTERSECT",EDGE,{"disambiguationData":[topologyDisambiguationEdgeConnected([makeQuery(id+"F2.opPattern","COPY",FACE,{"derivedFrom":makeQuery(id+"F1.opExtrude","SWEPT_FACE",FACE,{"disambiguationData":[OSD([sQuery(id+"F0.wireOp",EDGE,"E11")])]}),"instanceName":"27"})])],"derivedFrom":[subQ0,makeQuery(id+"F2.opPattern","COPY",FACE,{"derivedFrom":subQ0,"instanceName":"1"}),makeQuery(id+"F2.opPattern","COPY",FACE,{"derivedFrom":subQ0,"instanceName":"2"}),makeQuery(id+"F2.opPattern","COPY",FACE,{"derivedFrom":subQ0,"instanceName":"3"}),makeQuery(id+"F2.opPattern","COPY",FACE,{"derivedFrom":subQ0,"instanceName":"4"}),makeQuery(id+"F2.opPattern","COPY",FACE,{"derivedFrom":subQ0,"instanceName":"5"}),makeQuery(id+"F2.opPattern","COPY",FACE,{"derivedFrom":subQ0,"instanceName":"6"}),makeQuery(id+"F2.opPattern","COPY",FACE,{"derivedFrom":subQ0,"instanceName":"7"}),makeQuery(id+"F2.opPattern","COPY",FACE,{"derivedFrom":subQ0,"instanceName":"8"}),makeQuery(id+"F2.opPattern","COPY",FACE,{"derivedFrom":subQ0,"instanceName":"9"}),makeQuery(id+"F2.opPattern","COPY",FACE,{"derivedFrom":subQ0,"instanceName":"10"}),makeQuery(id+"F2.opPattern","COPY",FACE,{"derivedFrom":subQ0,"instanceName":"11"}),makeQuery(id+"F2.opPattern","COPY",FACE,{"derivedFrom":subQ0,"instanceName":"12"}),makeQuery(id+"F2.opPattern","COPY",FACE,{"derivedFrom":subQ0,"instanceName":"13"}),makeQuery(id+"F2.opPattern","COPY",FACE,{"derivedFrom":subQ0,"instanceName":"14"}),makeQuery(id+"F2.opPattern","COPY",FACE,{"derivedFrom":subQ0,"instanceName":"15"}),makeQuery(id+"F2.opPattern","COPY",FACE,{"derivedFrom":subQ0,"instanceName":"16"}),makeQuery(id+"F2.opPattern","COPY",FACE,{"derivedFrom":subQ0,"instanceName":"17"}),makeQuery(id+"F2.opPattern","COPY",FACE,{"derivedFrom":subQ0,"instanceName":"18"}),makeQuery(id+"F2.opPattern","COPY",FACE,{"derivedFrom":subQ0,"instanceName":"19"}),makeQuery(id+"F2.opPattern","COPY",FACE,{"derivedFrom":subQ0,"instanceName":"20"}),makeQuery(id+"F2.opPattern","COPY",FACE,{"derivedFrom":subQ0,"instanceName":"21"}),makeQuery(id+"F2.opPattern","COPY",FACE,{"derivedFrom":subQ0,"instanceName":"22"}),makeQuery(id+"F2.opPattern","COPY",FACE,{"derivedFrom":subQ0,"instanceName":"23"}),makeQuery(id+"F2.opPattern","COPY",FACE,{"derivedFrom":subQ0,"instanceName":"24"}),makeQuery(id+"F2.opPattern","COPY",FACE,{"derivedFrom":subQ0,"instanceName":"25"}),makeQuery(id+"F2.opPattern","COPY",FACE,{"derivedFrom":subQ0,"instanceName":"26"}),makeQuery(id+"F2.opPattern","COPY",FACE,{"derivedFrom":subQ0,"instanceName":"28"})]});}
            var Q18;
            {var subQ0=makeQuery(id+"F1.opExtrude","SWEPT_FACE",FACE,{"disambiguationData":[OSD([sQuery(id+"F0.wireOp",EDGE,"E0")])]});Q18=makeQuery(id+"F3.opBoolean","INTERSECT",EDGE,{"disambiguationData":[topologyDisambiguationEdgeConnected([makeQuery(id+"F2.opPattern","COPY",FACE,{"derivedFrom":makeQuery(id+"F1.opExtrude","SWEPT_FACE",FACE,{"disambiguationData":[OSD([sQuery(id+"F0.wireOp",EDGE,"E11")])]}),"instanceName":"28"})])],"derivedFrom":[subQ0,makeQuery(id+"F2.opPattern","COPY",FACE,{"derivedFrom":subQ0,"instanceName":"1"}),makeQuery(id+"F2.opPattern","COPY",FACE,{"derivedFrom":subQ0,"instanceName":"2"}),makeQuery(id+"F2.opPattern","COPY",FACE,{"derivedFrom":subQ0,"instanceName":"3"}),makeQuery(id+"F2.opPattern","COPY",FACE,{"derivedFrom":subQ0,"instanceName":"4"}),makeQuery(id+"F2.opPattern","COPY",FACE,{"derivedFrom":subQ0,"instanceName":"5"}),makeQuery(id+"F2.opPattern","COPY",FACE,{"derivedFrom":subQ0,"instanceName":"6"}),makeQuery(id+"F2.opPattern","COPY",FACE,{"derivedFrom":subQ0,"instanceName":"7"}),makeQuery(id+"F2.opPattern","COPY",FACE,{"derivedFrom":subQ0,"instanceName":"8"}),makeQuery(id+"F2.opPattern","COPY",FACE,{"derivedFrom":subQ0,"instanceName":"9"}),makeQuery(id+"F2.opPattern","COPY",FACE,{"derivedFrom":subQ0,"instanceName":"10"}),makeQuery(id+"F2.opPattern","COPY",FACE,{"derivedFrom":subQ0,"instanceName":"11"}),makeQuery(id+"F2.opPattern","COPY",FACE,{"derivedFrom":subQ0,"instanceName":"12"}),makeQuery(id+"F2.opPattern","COPY",FACE,{"derivedFrom":subQ0,"instanceName":"13"}),makeQuery(id+"F2.opPattern","COPY",FACE,{"derivedFrom":subQ0,"instanceName":"14"}),makeQuery(id+"F2.opPattern","COPY",FACE,{"derivedFrom":subQ0,"instanceName":"15"}),makeQuery(id+"F2.opPattern","COPY",FACE,{"derivedFrom":subQ0,"instanceName":"16"}),makeQuery(id+"F2.opPattern","COPY",FACE,{"derivedFrom":subQ0,"instanceName":"17"}),makeQuery(id+"F2.opPattern","COPY",FACE,{"derivedFrom":subQ0,"instanceName":"18"}),makeQuery(id+"F2.opPattern","COPY",FACE,{"derivedFrom":subQ0,"instanceName":"19"}),makeQuery(id+"F2.opPattern","COPY",FACE,{"derivedFrom":subQ0,"instanceName":"20"}),makeQuery(id+"F2.opPattern","COPY",FACE,{"derivedFrom":subQ0,"instanceName":"21"}),makeQuery(id+"F2.opPattern","COPY",FACE,{"derivedFrom":subQ0,"instanceName":"22"}),makeQuery(id+"F2.opPattern","COPY",FACE,{"derivedFrom":subQ0,"instanceName":"23"}),makeQuery(id+"F2.opPattern","COPY",FACE,{"derivedFrom":subQ0,"instanceName":"24"}),makeQuery(id+"F2.opPattern","COPY",FACE,{"derivedFrom":subQ0,"instanceName":"25"}),makeQuery(id+"F2.opPattern","COPY",FACE,{"derivedFrom":subQ0,"instanceName":"26"}),makeQuery(id+"F2.opPattern","COPY",FACE,{"derivedFrom":subQ0,"instanceName":"27"}),makeQuery(id+"F2.opPattern","COPY",FACE,{"derivedFrom":subQ0,"instanceName":"29"})]});}
            var Q19;
            {var subQ0=makeQuery(id+"F1.opExtrude","SWEPT_FACE",FACE,{"disambiguationData":[OSD([sQuery(id+"F0.wireOp",EDGE,"E0")])]});Q19=makeQuery(id+"F3.opBoolean","INTERSECT",EDGE,{"disambiguationData":[topologyDisambiguationEdgeConnected([makeQuery(id+"F2.opPattern","COPY",FACE,{"derivedFrom":makeQuery(id+"F1.opExtrude","SWEPT_FACE",FACE,{"disambiguationData":[OSD([sQuery(id+"F0.wireOp",EDGE,"E11")])]}),"instanceName":"29"})])],"derivedFrom":[subQ0,makeQuery(id+"F2.opPattern","COPY",FACE,{"derivedFrom":subQ0,"instanceName":"1"}),makeQuery(id+"F2.opPattern","COPY",FACE,{"derivedFrom":subQ0,"instanceName":"2"}),makeQuery(id+"F2.opPattern","COPY",FACE,{"derivedFrom":subQ0,"instanceName":"3"}),makeQuery(id+"F2.opPattern","COPY",FACE,{"derivedFrom":subQ0,"instanceName":"4"}),makeQuery(id+"F2.opPattern","COPY",FACE,{"derivedFrom":subQ0,"instanceName":"5"}),makeQuery(id+"F2.opPattern","COPY",FACE,{"derivedFrom":subQ0,"instanceName":"6"}),makeQuery(id+"F2.opPattern","COPY",FACE,{"derivedFrom":subQ0,"instanceName":"7"}),makeQuery(id+"F2.opPattern","COPY",FACE,{"derivedFrom":subQ0,"instanceName":"8"}),makeQuery(id+"F2.opPattern","COPY",FACE,{"derivedFrom":subQ0,"instanceName":"9"}),makeQuery(id+"F2.opPattern","COPY",FACE,{"derivedFrom":subQ0,"instanceName":"10"}),makeQuery(id+"F2.opPattern","COPY",FACE,{"derivedFrom":subQ0,"instanceName":"11"}),makeQuery(id+"F2.opPattern","COPY",FACE,{"derivedFrom":subQ0,"instanceName":"12"}),makeQuery(id+"F2.opPattern","COPY",FACE,{"derivedFrom":subQ0,"instanceName":"13"}),makeQuery(id+"F2.opPattern","COPY",FACE,{"derivedFrom":subQ0,"instanceName":"14"}),makeQuery(id+"F2.opPattern","COPY",FACE,{"derivedFrom":subQ0,"instanceName":"15"}),makeQuery(id+"F2.opPattern","COPY",FACE,{"derivedFrom":subQ0,"instanceName":"16"}),makeQuery(id+"F2.opPattern","COPY",FACE,{"derivedFrom":subQ0,"instanceName":"17"}),makeQuery(id+"F2.opPattern","COPY",FACE,{"derivedFrom":subQ0,"instanceName":"18"}),makeQuery(id+"F2.opPattern","COPY",FACE,{"derivedFrom":subQ0,"instanceName":"19"}),makeQuery(id+"F2.opPattern","COPY",FACE,{"derivedFrom":subQ0,"instanceName":"20"}),makeQuery(id+"F2.opPattern","COPY",FACE,{"derivedFrom":subQ0,"instanceName":"21"}),makeQuery(id+"F2.opPattern","COPY",FACE,{"derivedFrom":subQ0,"instanceName":"22"}),makeQuery(id+"F2.opPattern","COPY",FACE,{"derivedFrom":subQ0,"instanceName":"23"}),makeQuery(id+"F2.opPattern","COPY",FACE,{"derivedFrom":subQ0,"instanceName":"24"}),makeQuery(id+"F2.opPattern","COPY",FACE,{"derivedFrom":subQ0,"instanceName":"25"}),makeQuery(id+"F2.opPattern","COPY",FACE,{"derivedFrom":subQ0,"instanceName":"26"}),makeQuery(id+"F2.opPattern","COPY",FACE,{"derivedFrom":subQ0,"instanceName":"27"}),makeQuery(id+"F2.opPattern","COPY",FACE,{"derivedFrom":subQ0,"instanceName":"28"})]});}
            var Q20;
            Q20=makeQuery(id+"F1.opExtrude","SWEPT_EDGE",EDGE,{"disambiguationData":[OSD([sQuery(id+"F0.wireOp",EDGE,"E0"),sQuery(id+"F0.wireOp",EDGE,"E11")])]});
            var Q21;
            {var subQ0=makeQuery(id+"F1.opExtrude","SWEPT_FACE",FACE,{"disambiguationData":[OSD([sQuery(id+"F0.wireOp",EDGE,"E0")])]});Q21=makeQuery(id+"F3.opBoolean","INTERSECT",EDGE,{"disambiguationData":[topologyDisambiguationEdgeConnected([makeQuery(id+"F2.opPattern","COPY",FACE,{"derivedFrom":makeQuery(id+"F1.opExtrude","SWEPT_FACE",FACE,{"disambiguationData":[OSD([sQuery(id+"F0.wireOp",EDGE,"E11")])]}),"instanceName":"1"})])],"derivedFrom":[subQ0,makeQuery(id+"F2.opPattern","COPY",FACE,{"derivedFrom":subQ0,"instanceName":"2"})]});}
            var Q22;
            {var subQ0=makeQuery(id+"F1.opExtrude","SWEPT_FACE",FACE,{"disambiguationData":[OSD([sQuery(id+"F0.wireOp",EDGE,"E0")])]});Q22=makeQuery(id+"F3.opBoolean","INTERSECT",EDGE,{"disambiguationData":[topologyDisambiguationEdgeConnected([makeQuery(id+"F2.opPattern","COPY",FACE,{"derivedFrom":makeQuery(id+"F1.opExtrude","SWEPT_FACE",FACE,{"disambiguationData":[OSD([sQuery(id+"F0.wireOp",EDGE,"E11")])]}),"instanceName":"2"})])],"derivedFrom":[subQ0,makeQuery(id+"F2.opPattern","COPY",FACE,{"derivedFrom":subQ0,"instanceName":"1"}),makeQuery(id+"F2.opPattern","COPY",FACE,{"derivedFrom":subQ0,"instanceName":"4"})]});}
            var Q23;
            {var subQ0=makeQuery(id+"F1.opExtrude","SWEPT_FACE",FACE,{"disambiguationData":[OSD([sQuery(id+"F0.wireOp",EDGE,"E0")])]});Q23=makeQuery(id+"F3.opBoolean","INTERSECT",EDGE,{"disambiguationData":[topologyDisambiguationEdgeConnected([makeQuery(id+"F2.opPattern","COPY",FACE,{"derivedFrom":makeQuery(id+"F1.opExtrude","SWEPT_FACE",FACE,{"disambiguationData":[OSD([sQuery(id+"F0.wireOp",EDGE,"E11")])]}),"instanceName":"3"})])],"derivedFrom":[subQ0,makeQuery(id+"F2.opPattern","COPY",FACE,{"derivedFrom":subQ0,"instanceName":"1"}),makeQuery(id+"F2.opPattern","COPY",FACE,{"derivedFrom":subQ0,"instanceName":"2"}),makeQuery(id+"F2.opPattern","COPY",FACE,{"derivedFrom":subQ0,"instanceName":"4"}),makeQuery(id+"F2.opPattern","COPY",FACE,{"derivedFrom":subQ0,"instanceName":"6"})]});}
            var Q24;
            {var subQ0=makeQuery(id+"F1.opExtrude","SWEPT_FACE",FACE,{"disambiguationData":[OSD([sQuery(id+"F0.wireOp",EDGE,"E0")])]});Q24=makeQuery(id+"F3.opBoolean","INTERSECT",EDGE,{"disambiguationData":[topologyDisambiguationEdgeConnected([makeQuery(id+"F2.opPattern","COPY",FACE,{"derivedFrom":makeQuery(id+"F1.opExtrude","SWEPT_FACE",FACE,{"disambiguationData":[OSD([sQuery(id+"F0.wireOp",EDGE,"E12.MirrorCS")])]}),"instanceName":"3"})])],"derivedFrom":[subQ0,makeQuery(id+"F2.opPattern","COPY",FACE,{"derivedFrom":subQ0,"instanceName":"1"}),makeQuery(id+"F2.opPattern","COPY",FACE,{"derivedFrom":subQ0,"instanceName":"2"}),makeQuery(id+"F2.opPattern","COPY",FACE,{"derivedFrom":subQ0,"instanceName":"4"}),makeQuery(id+"F2.opPattern","COPY",FACE,{"derivedFrom":subQ0,"instanceName":"6"})]});}
            var Q25;
            {var subQ0=makeQuery(id+"F1.opExtrude","SWEPT_FACE",FACE,{"disambiguationData":[OSD([sQuery(id+"F0.wireOp",EDGE,"E0")])]});Q25=makeQuery(id+"F3.opBoolean","INTERSECT",EDGE,{"disambiguationData":[topologyDisambiguationEdgeConnected([makeQuery(id+"F2.opPattern","COPY",FACE,{"derivedFrom":makeQuery(id+"F1.opExtrude","SWEPT_FACE",FACE,{"disambiguationData":[OSD([sQuery(id+"F0.wireOp",EDGE,"E12.MirrorCS")])]}),"instanceName":"4"})])],"derivedFrom":[subQ0,makeQuery(id+"F2.opPattern","COPY",FACE,{"derivedFrom":subQ0,"instanceName":"1"}),makeQuery(id+"F2.opPattern","COPY",FACE,{"derivedFrom":subQ0,"instanceName":"2"}),makeQuery(id+"F2.opPattern","COPY",FACE,{"derivedFrom":subQ0,"instanceName":"3"})]});}
            var Q26;
            {var subQ0=makeQuery(id+"F1.opExtrude","SWEPT_FACE",FACE,{"disambiguationData":[OSD([sQuery(id+"F0.wireOp",EDGE,"E0")])]});Q26=makeQuery(id+"F3.opBoolean","INTERSECT",EDGE,{"disambiguationData":[topologyDisambiguationEdgeConnected([makeQuery(id+"F2.opPattern","COPY",FACE,{"derivedFrom":makeQuery(id+"F1.opExtrude","SWEPT_FACE",FACE,{"disambiguationData":[OSD([sQuery(id+"F0.wireOp",EDGE,"E12.MirrorCS")])]}),"instanceName":"5"})])],"derivedFrom":[subQ0,makeQuery(id+"F2.opPattern","COPY",FACE,{"derivedFrom":subQ0,"instanceName":"1"}),makeQuery(id+"F2.opPattern","COPY",FACE,{"derivedFrom":subQ0,"instanceName":"2"}),makeQuery(id+"F2.opPattern","COPY",FACE,{"derivedFrom":subQ0,"instanceName":"3"}),makeQuery(id+"F2.opPattern","COPY",FACE,{"derivedFrom":subQ0,"instanceName":"4"}),makeQuery(id+"F2.opPattern","COPY",FACE,{"derivedFrom":subQ0,"instanceName":"6"}),makeQuery(id+"F2.opPattern","COPY",FACE,{"derivedFrom":subQ0,"instanceName":"7"})]});}
            var Q27;
            {var subQ0=makeQuery(id+"F1.opExtrude","SWEPT_FACE",FACE,{"disambiguationData":[OSD([sQuery(id+"F0.wireOp",EDGE,"E0")])]});Q27=makeQuery(id+"F3.opBoolean","INTERSECT",EDGE,{"disambiguationData":[topologyDisambiguationEdgeConnected([makeQuery(id+"F2.opPattern","COPY",FACE,{"derivedFrom":makeQuery(id+"F1.opExtrude","SWEPT_FACE",FACE,{"disambiguationData":[OSD([sQuery(id+"F0.wireOp",EDGE,"E12.MirrorCS")])]}),"instanceName":"6"})])],"derivedFrom":[subQ0,makeQuery(id+"F2.opPattern","COPY",FACE,{"derivedFrom":subQ0,"instanceName":"1"}),makeQuery(id+"F2.opPattern","COPY",FACE,{"derivedFrom":subQ0,"instanceName":"2"}),makeQuery(id+"F2.opPattern","COPY",FACE,{"derivedFrom":subQ0,"instanceName":"3"}),makeQuery(id+"F2.opPattern","COPY",FACE,{"derivedFrom":subQ0,"instanceName":"4"}),makeQuery(id+"F2.opPattern","COPY",FACE,{"derivedFrom":subQ0,"instanceName":"5"})]});}
            var Q28;
            {var subQ0=makeQuery(id+"F1.opExtrude","SWEPT_FACE",FACE,{"disambiguationData":[OSD([sQuery(id+"F0.wireOp",EDGE,"E0")])]});Q28=makeQuery(id+"F3.opBoolean","INTERSECT",EDGE,{"disambiguationData":[topologyDisambiguationEdgeConnected([makeQuery(id+"F2.opPattern","COPY",FACE,{"derivedFrom":makeQuery(id+"F1.opExtrude","SWEPT_FACE",FACE,{"disambiguationData":[OSD([sQuery(id+"F0.wireOp",EDGE,"E12.MirrorCS")])]}),"instanceName":"7"})])],"derivedFrom":[subQ0,makeQuery(id+"F2.opPattern","COPY",FACE,{"derivedFrom":subQ0,"instanceName":"1"}),makeQuery(id+"F2.opPattern","COPY",FACE,{"derivedFrom":subQ0,"instanceName":"2"}),makeQuery(id+"F2.opPattern","COPY",FACE,{"derivedFrom":subQ0,"instanceName":"3"}),makeQuery(id+"F2.opPattern","COPY",FACE,{"derivedFrom":subQ0,"instanceName":"4"}),makeQuery(id+"F2.opPattern","COPY",FACE,{"derivedFrom":subQ0,"instanceName":"5"}),makeQuery(id+"F2.opPattern","COPY",FACE,{"derivedFrom":subQ0,"instanceName":"6"}),makeQuery(id+"F2.opPattern","COPY",FACE,{"derivedFrom":subQ0,"instanceName":"8"})]});}
            var Q29;
            {var subQ0=makeQuery(id+"F1.opExtrude","SWEPT_FACE",FACE,{"disambiguationData":[OSD([sQuery(id+"F0.wireOp",EDGE,"E0")])]});Q29=makeQuery(id+"F3.opBoolean","INTERSECT",EDGE,{"disambiguationData":[topologyDisambiguationEdgeConnected([makeQuery(id+"F2.opPattern","COPY",FACE,{"derivedFrom":makeQuery(id+"F1.opExtrude","SWEPT_FACE",FACE,{"disambiguationData":[OSD([sQuery(id+"F0.wireOp",EDGE,"E12.MirrorCS")])]}),"instanceName":"8"})])],"derivedFrom":[subQ0,makeQuery(id+"F2.opPattern","COPY",FACE,{"derivedFrom":subQ0,"instanceName":"1"}),makeQuery(id+"F2.opPattern","COPY",FACE,{"derivedFrom":subQ0,"instanceName":"2"}),makeQuery(id+"F2.opPattern","COPY",FACE,{"derivedFrom":subQ0,"instanceName":"3"}),makeQuery(id+"F2.opPattern","COPY",FACE,{"derivedFrom":subQ0,"instanceName":"4"}),makeQuery(id+"F2.opPattern","COPY",FACE,{"derivedFrom":subQ0,"instanceName":"5"}),makeQuery(id+"F2.opPattern","COPY",FACE,{"derivedFrom":subQ0,"instanceName":"6"}),makeQuery(id+"F2.opPattern","COPY",FACE,{"derivedFrom":subQ0,"instanceName":"7"}),makeQuery(id+"F2.opPattern","COPY",FACE,{"derivedFrom":subQ0,"instanceName":"9"})]});}
            var Q30;
            {var subQ0=makeQuery(id+"F1.opExtrude","SWEPT_FACE",FACE,{"disambiguationData":[OSD([sQuery(id+"F0.wireOp",EDGE,"E0")])]});Q30=makeQuery(id+"F3.opBoolean","INTERSECT",EDGE,{"disambiguationData":[topologyDisambiguationEdgeConnected([makeQuery(id+"F2.opPattern","COPY",FACE,{"derivedFrom":makeQuery(id+"F1.opExtrude","SWEPT_FACE",FACE,{"disambiguationData":[OSD([sQuery(id+"F0.wireOp",EDGE,"E11")])]}),"instanceName":"5"})])],"derivedFrom":[subQ0,makeQuery(id+"F2.opPattern","COPY",FACE,{"derivedFrom":subQ0,"instanceName":"1"}),makeQuery(id+"F2.opPattern","COPY",FACE,{"derivedFrom":subQ0,"instanceName":"2"}),makeQuery(id+"F2.opPattern","COPY",FACE,{"derivedFrom":subQ0,"instanceName":"3"}),makeQuery(id+"F2.opPattern","COPY",FACE,{"derivedFrom":subQ0,"instanceName":"4"}),makeQuery(id+"F2.opPattern","COPY",FACE,{"derivedFrom":subQ0,"instanceName":"6"}),makeQuery(id+"F2.opPattern","COPY",FACE,{"derivedFrom":subQ0,"instanceName":"7"})]});}
            var Q31;
            {var subQ0=makeQuery(id+"F1.opExtrude","SWEPT_FACE",FACE,{"disambiguationData":[OSD([sQuery(id+"F0.wireOp",EDGE,"E0")])]});Q31=makeQuery(id+"F3.opBoolean","INTERSECT",EDGE,{"disambiguationData":[topologyDisambiguationEdgeConnected([makeQuery(id+"F2.opPattern","COPY",FACE,{"derivedFrom":makeQuery(id+"F1.opExtrude","SWEPT_FACE",FACE,{"disambiguationData":[OSD([sQuery(id+"F0.wireOp",EDGE,"E11")])]}),"instanceName":"6"})])],"derivedFrom":[subQ0,makeQuery(id+"F2.opPattern","COPY",FACE,{"derivedFrom":subQ0,"instanceName":"1"}),makeQuery(id+"F2.opPattern","COPY",FACE,{"derivedFrom":subQ0,"instanceName":"2"}),makeQuery(id+"F2.opPattern","COPY",FACE,{"derivedFrom":subQ0,"instanceName":"3"}),makeQuery(id+"F2.opPattern","COPY",FACE,{"derivedFrom":subQ0,"instanceName":"4"}),makeQuery(id+"F2.opPattern","COPY",FACE,{"derivedFrom":subQ0,"instanceName":"5"})]});}
            var Q32;
            {var subQ0=makeQuery(id+"F1.opExtrude","SWEPT_FACE",FACE,{"disambiguationData":[OSD([sQuery(id+"F0.wireOp",EDGE,"E0")])]});Q32=makeQuery(id+"F3.opBoolean","INTERSECT",EDGE,{"disambiguationData":[topologyDisambiguationEdgeConnected([makeQuery(id+"F2.opPattern","COPY",FACE,{"derivedFrom":makeQuery(id+"F1.opExtrude","SWEPT_FACE",FACE,{"disambiguationData":[OSD([sQuery(id+"F0.wireOp",EDGE,"E11")])]}),"instanceName":"7"})])],"derivedFrom":[subQ0,makeQuery(id+"F2.opPattern","COPY",FACE,{"derivedFrom":subQ0,"instanceName":"1"}),makeQuery(id+"F2.opPattern","COPY",FACE,{"derivedFrom":subQ0,"instanceName":"2"}),makeQuery(id+"F2.opPattern","COPY",FACE,{"derivedFrom":subQ0,"instanceName":"3"}),makeQuery(id+"F2.opPattern","COPY",FACE,{"derivedFrom":subQ0,"instanceName":"4"}),makeQuery(id+"F2.opPattern","COPY",FACE,{"derivedFrom":subQ0,"instanceName":"5"}),makeQuery(id+"F2.opPattern","COPY",FACE,{"derivedFrom":subQ0,"instanceName":"6"}),makeQuery(id+"F2.opPattern","COPY",FACE,{"derivedFrom":subQ0,"instanceName":"8"})]});}
            var Q33;
            {var subQ0=makeQuery(id+"F1.opExtrude","SWEPT_FACE",FACE,{"disambiguationData":[OSD([sQuery(id+"F0.wireOp",EDGE,"E0")])]});Q33=makeQuery(id+"F3.opBoolean","INTERSECT",EDGE,{"disambiguationData":[topologyDisambiguationEdgeConnected([makeQuery(id+"F2.opPattern","COPY",FACE,{"derivedFrom":makeQuery(id+"F1.opExtrude","SWEPT_FACE",FACE,{"disambiguationData":[OSD([sQuery(id+"F0.wireOp",EDGE,"E11")])]}),"instanceName":"8"})])],"derivedFrom":[subQ0,makeQuery(id+"F2.opPattern","COPY",FACE,{"derivedFrom":subQ0,"instanceName":"1"}),makeQuery(id+"F2.opPattern","COPY",FACE,{"derivedFrom":subQ0,"instanceName":"2"}),makeQuery(id+"F2.opPattern","COPY",FACE,{"derivedFrom":subQ0,"instanceName":"3"}),makeQuery(id+"F2.opPattern","COPY",FACE,{"derivedFrom":subQ0,"instanceName":"4"}),makeQuery(id+"F2.opPattern","COPY",FACE,{"derivedFrom":subQ0,"instanceName":"5"}),makeQuery(id+"F2.opPattern","COPY",FACE,{"derivedFrom":subQ0,"instanceName":"6"}),makeQuery(id+"F2.opPattern","COPY",FACE,{"derivedFrom":subQ0,"instanceName":"7"}),makeQuery(id+"F2.opPattern","COPY",FACE,{"derivedFrom":subQ0,"instanceName":"9"})]});}
            var Q34;
            {var subQ0=makeQuery(id+"F1.opExtrude","SWEPT_FACE",FACE,{"disambiguationData":[OSD([sQuery(id+"F0.wireOp",EDGE,"E0")])]});Q34=makeQuery(id+"F3.opBoolean","INTERSECT",EDGE,{"disambiguationData":[topologyDisambiguationEdgeConnected([makeQuery(id+"F2.opPattern","COPY",FACE,{"derivedFrom":makeQuery(id+"F1.opExtrude","SWEPT_FACE",FACE,{"disambiguationData":[OSD([sQuery(id+"F0.wireOp",EDGE,"E12.MirrorCS")])]}),"instanceName":"9"})])],"derivedFrom":[subQ0,makeQuery(id+"F2.opPattern","COPY",FACE,{"derivedFrom":subQ0,"instanceName":"1"}),makeQuery(id+"F2.opPattern","COPY",FACE,{"derivedFrom":subQ0,"instanceName":"2"}),makeQuery(id+"F2.opPattern","COPY",FACE,{"derivedFrom":subQ0,"instanceName":"3"}),makeQuery(id+"F2.opPattern","COPY",FACE,{"derivedFrom":subQ0,"instanceName":"4"}),makeQuery(id+"F2.opPattern","COPY",FACE,{"derivedFrom":subQ0,"instanceName":"5"}),makeQuery(id+"F2.opPattern","COPY",FACE,{"derivedFrom":subQ0,"instanceName":"6"}),makeQuery(id+"F2.opPattern","COPY",FACE,{"derivedFrom":subQ0,"instanceName":"7"}),makeQuery(id+"F2.opPattern","COPY",FACE,{"derivedFrom":subQ0,"instanceName":"8"}),makeQuery(id+"F2.opPattern","COPY",FACE,{"derivedFrom":subQ0,"instanceName":"10"})]});}
            var Q35;
            {var subQ0=makeQuery(id+"F1.opExtrude","SWEPT_FACE",FACE,{"disambiguationData":[OSD([sQuery(id+"F0.wireOp",EDGE,"E0")])]});Q35=makeQuery(id+"F3.opBoolean","INTERSECT",EDGE,{"disambiguationData":[topologyDisambiguationEdgeConnected([makeQuery(id+"F2.opPattern","COPY",FACE,{"derivedFrom":makeQuery(id+"F1.opExtrude","SWEPT_FACE",FACE,{"disambiguationData":[OSD([sQuery(id+"F0.wireOp",EDGE,"E11")])]}),"instanceName":"9"})])],"derivedFrom":[subQ0,makeQuery(id+"F2.opPattern","COPY",FACE,{"derivedFrom":subQ0,"instanceName":"1"}),makeQuery(id+"F2.opPattern","COPY",FACE,{"derivedFrom":subQ0,"instanceName":"2"}),makeQuery(id+"F2.opPattern","COPY",FACE,{"derivedFrom":subQ0,"instanceName":"3"}),makeQuery(id+"F2.opPattern","COPY",FACE,{"derivedFrom":subQ0,"instanceName":"4"}),makeQuery(id+"F2.opPattern","COPY",FACE,{"derivedFrom":subQ0,"instanceName":"5"}),makeQuery(id+"F2.opPattern","COPY",FACE,{"derivedFrom":subQ0,"instanceName":"6"}),makeQuery(id+"F2.opPattern","COPY",FACE,{"derivedFrom":subQ0,"instanceName":"7"}),makeQuery(id+"F2.opPattern","COPY",FACE,{"derivedFrom":subQ0,"instanceName":"8"}),makeQuery(id+"F2.opPattern","COPY",FACE,{"derivedFrom":subQ0,"instanceName":"10"})]});}
            var Q36;
            {var subQ0=makeQuery(id+"F1.opExtrude","SWEPT_FACE",FACE,{"disambiguationData":[OSD([sQuery(id+"F0.wireOp",EDGE,"E0")])]});Q36=makeQuery(id+"F3.opBoolean","INTERSECT",EDGE,{"disambiguationData":[topologyDisambiguationEdgeConnected([makeQuery(id+"F2.opPattern","COPY",FACE,{"derivedFrom":makeQuery(id+"F1.opExtrude","SWEPT_FACE",FACE,{"disambiguationData":[OSD([sQuery(id+"F0.wireOp",EDGE,"E12.MirrorCS")])]}),"instanceName":"10"})])],"derivedFrom":[subQ0,makeQuery(id+"F2.opPattern","COPY",FACE,{"derivedFrom":subQ0,"instanceName":"1"}),makeQuery(id+"F2.opPattern","COPY",FACE,{"derivedFrom":subQ0,"instanceName":"2"}),makeQuery(id+"F2.opPattern","COPY",FACE,{"derivedFrom":subQ0,"instanceName":"3"}),makeQuery(id+"F2.opPattern","COPY",FACE,{"derivedFrom":subQ0,"instanceName":"4"}),makeQuery(id+"F2.opPattern","COPY",FACE,{"derivedFrom":subQ0,"instanceName":"5"}),makeQuery(id+"F2.opPattern","COPY",FACE,{"derivedFrom":subQ0,"instanceName":"6"}),makeQuery(id+"F2.opPattern","COPY",FACE,{"derivedFrom":subQ0,"instanceName":"7"}),makeQuery(id+"F2.opPattern","COPY",FACE,{"derivedFrom":subQ0,"instanceName":"8"}),makeQuery(id+"F2.opPattern","COPY",FACE,{"derivedFrom":subQ0,"instanceName":"9"}),makeQuery(id+"F2.opPattern","COPY",FACE,{"derivedFrom":subQ0,"instanceName":"11"})]});}
            var Q37;
            {var subQ0=makeQuery(id+"F1.opExtrude","SWEPT_FACE",FACE,{"disambiguationData":[OSD([sQuery(id+"F0.wireOp",EDGE,"E0")])]});Q37=makeQuery(id+"F3.opBoolean","INTERSECT",EDGE,{"disambiguationData":[topologyDisambiguationEdgeConnected([makeQuery(id+"F2.opPattern","COPY",FACE,{"derivedFrom":makeQuery(id+"F1.opExtrude","SWEPT_FACE",FACE,{"disambiguationData":[OSD([sQuery(id+"F0.wireOp",EDGE,"E11")])]}),"instanceName":"10"})])],"derivedFrom":[subQ0,makeQuery(id+"F2.opPattern","COPY",FACE,{"derivedFrom":subQ0,"instanceName":"1"}),makeQuery(id+"F2.opPattern","COPY",FACE,{"derivedFrom":subQ0,"instanceName":"2"}),makeQuery(id+"F2.opPattern","COPY",FACE,{"derivedFrom":subQ0,"instanceName":"3"}),makeQuery(id+"F2.opPattern","COPY",FACE,{"derivedFrom":subQ0,"instanceName":"4"}),makeQuery(id+"F2.opPattern","COPY",FACE,{"derivedFrom":subQ0,"instanceName":"5"}),makeQuery(id+"F2.opPattern","COPY",FACE,{"derivedFrom":subQ0,"instanceName":"6"}),makeQuery(id+"F2.opPattern","COPY",FACE,{"derivedFrom":subQ0,"instanceName":"7"}),makeQuery(id+"F2.opPattern","COPY",FACE,{"derivedFrom":subQ0,"instanceName":"8"}),makeQuery(id+"F2.opPattern","COPY",FACE,{"derivedFrom":subQ0,"instanceName":"9"}),makeQuery(id+"F2.opPattern","COPY",FACE,{"derivedFrom":subQ0,"instanceName":"11"})]});}
            var Q38;
            {var subQ0=makeQuery(id+"F1.opExtrude","SWEPT_FACE",FACE,{"disambiguationData":[OSD([sQuery(id+"F0.wireOp",EDGE,"E0")])]});Q38=makeQuery(id+"F3.opBoolean","INTERSECT",EDGE,{"disambiguationData":[topologyDisambiguationEdgeConnected([makeQuery(id+"F2.opPattern","COPY",FACE,{"derivedFrom":makeQuery(id+"F1.opExtrude","SWEPT_FACE",FACE,{"disambiguationData":[OSD([sQuery(id+"F0.wireOp",EDGE,"E12.MirrorCS")])]}),"instanceName":"11"})])],"derivedFrom":[subQ0,makeQuery(id+"F2.opPattern","COPY",FACE,{"derivedFrom":subQ0,"instanceName":"1"}),makeQuery(id+"F2.opPattern","COPY",FACE,{"derivedFrom":subQ0,"instanceName":"2"}),makeQuery(id+"F2.opPattern","COPY",FACE,{"derivedFrom":subQ0,"instanceName":"3"}),makeQuery(id+"F2.opPattern","COPY",FACE,{"derivedFrom":subQ0,"instanceName":"4"}),makeQuery(id+"F2.opPattern","COPY",FACE,{"derivedFrom":subQ0,"instanceName":"5"}),makeQuery(id+"F2.opPattern","COPY",FACE,{"derivedFrom":subQ0,"instanceName":"6"}),makeQuery(id+"F2.opPattern","COPY",FACE,{"derivedFrom":subQ0,"instanceName":"7"}),makeQuery(id+"F2.opPattern","COPY",FACE,{"derivedFrom":subQ0,"instanceName":"8"}),makeQuery(id+"F2.opPattern","COPY",FACE,{"derivedFrom":subQ0,"instanceName":"9"}),makeQuery(id+"F2.opPattern","COPY",FACE,{"derivedFrom":subQ0,"instanceName":"10"}),makeQuery(id+"F2.opPattern","COPY",FACE,{"derivedFrom":subQ0,"instanceName":"12"})]});}
            var Q39;
            {var subQ0=makeQuery(id+"F1.opExtrude","SWEPT_FACE",FACE,{"disambiguationData":[OSD([sQuery(id+"F0.wireOp",EDGE,"E0")])]});Q39=makeQuery(id+"F3.opBoolean","INTERSECT",EDGE,{"disambiguationData":[topologyDisambiguationEdgeConnected([makeQuery(id+"F2.opPattern","COPY",FACE,{"derivedFrom":makeQuery(id+"F1.opExtrude","SWEPT_FACE",FACE,{"disambiguationData":[OSD([sQuery(id+"F0.wireOp",EDGE,"E12.MirrorCS")])]}),"instanceName":"12"})])],"derivedFrom":[subQ0,makeQuery(id+"F2.opPattern","COPY",FACE,{"derivedFrom":subQ0,"instanceName":"1"}),makeQuery(id+"F2.opPattern","COPY",FACE,{"derivedFrom":subQ0,"instanceName":"2"}),makeQuery(id+"F2.opPattern","COPY",FACE,{"derivedFrom":subQ0,"instanceName":"3"}),makeQuery(id+"F2.opPattern","COPY",FACE,{"derivedFrom":subQ0,"instanceName":"4"}),makeQuery(id+"F2.opPattern","COPY",FACE,{"derivedFrom":subQ0,"instanceName":"5"}),makeQuery(id+"F2.opPattern","COPY",FACE,{"derivedFrom":subQ0,"instanceName":"6"}),makeQuery(id+"F2.opPattern","COPY",FACE,{"derivedFrom":subQ0,"instanceName":"7"}),makeQuery(id+"F2.opPattern","COPY",FACE,{"derivedFrom":subQ0,"instanceName":"8"}),makeQuery(id+"F2.opPattern","COPY",FACE,{"derivedFrom":subQ0,"instanceName":"9"}),makeQuery(id+"F2.opPattern","COPY",FACE,{"derivedFrom":subQ0,"instanceName":"10"}),makeQuery(id+"F2.opPattern","COPY",FACE,{"derivedFrom":subQ0,"instanceName":"11"}),makeQuery(id+"F2.opPattern","COPY",FACE,{"derivedFrom":subQ0,"instanceName":"13"})]});}
            var Q40;
            {var subQ0=makeQuery(id+"F1.opExtrude","SWEPT_FACE",FACE,{"disambiguationData":[OSD([sQuery(id+"F0.wireOp",EDGE,"E0")])]});Q40=makeQuery(id+"F3.opBoolean","INTERSECT",EDGE,{"disambiguationData":[topologyDisambiguationEdgeConnected([makeQuery(id+"F2.opPattern","COPY",FACE,{"derivedFrom":makeQuery(id+"F1.opExtrude","SWEPT_FACE",FACE,{"disambiguationData":[OSD([sQuery(id+"F0.wireOp",EDGE,"E12.MirrorCS")])]}),"instanceName":"13"})])],"derivedFrom":[subQ0,makeQuery(id+"F2.opPattern","COPY",FACE,{"derivedFrom":subQ0,"instanceName":"1"}),makeQuery(id+"F2.opPattern","COPY",FACE,{"derivedFrom":subQ0,"instanceName":"2"}),makeQuery(id+"F2.opPattern","COPY",FACE,{"derivedFrom":subQ0,"instanceName":"3"}),makeQuery(id+"F2.opPattern","COPY",FACE,{"derivedFrom":subQ0,"instanceName":"4"}),makeQuery(id+"F2.opPattern","COPY",FACE,{"derivedFrom":subQ0,"instanceName":"5"}),makeQuery(id+"F2.opPattern","COPY",FACE,{"derivedFrom":subQ0,"instanceName":"6"}),makeQuery(id+"F2.opPattern","COPY",FACE,{"derivedFrom":subQ0,"instanceName":"7"}),makeQuery(id+"F2.opPattern","COPY",FACE,{"derivedFrom":subQ0,"instanceName":"8"}),makeQuery(id+"F2.opPattern","COPY",FACE,{"derivedFrom":subQ0,"instanceName":"9"}),makeQuery(id+"F2.opPattern","COPY",FACE,{"derivedFrom":subQ0,"instanceName":"10"}),makeQuery(id+"F2.opPattern","COPY",FACE,{"derivedFrom":subQ0,"instanceName":"11"}),makeQuery(id+"F2.opPattern","COPY",FACE,{"derivedFrom":subQ0,"instanceName":"12"}),makeQuery(id+"F2.opPattern","COPY",FACE,{"derivedFrom":subQ0,"instanceName":"14"})]});}
            var Q41;
            {var subQ0=makeQuery(id+"F1.opExtrude","SWEPT_FACE",FACE,{"disambiguationData":[OSD([sQuery(id+"F0.wireOp",EDGE,"E0")])]});Q41=makeQuery(id+"F3.opBoolean","INTERSECT",EDGE,{"disambiguationData":[topologyDisambiguationEdgeConnected([makeQuery(id+"F2.opPattern","COPY",FACE,{"derivedFrom":makeQuery(id+"F1.opExtrude","SWEPT_FACE",FACE,{"disambiguationData":[OSD([sQuery(id+"F0.wireOp",EDGE,"E12.MirrorCS")])]}),"instanceName":"14"})])],"derivedFrom":[subQ0,makeQuery(id+"F2.opPattern","COPY",FACE,{"derivedFrom":subQ0,"instanceName":"1"}),makeQuery(id+"F2.opPattern","COPY",FACE,{"derivedFrom":subQ0,"instanceName":"2"}),makeQuery(id+"F2.opPattern","COPY",FACE,{"derivedFrom":subQ0,"instanceName":"3"}),makeQuery(id+"F2.opPattern","COPY",FACE,{"derivedFrom":subQ0,"instanceName":"4"}),makeQuery(id+"F2.opPattern","COPY",FACE,{"derivedFrom":subQ0,"instanceName":"5"}),makeQuery(id+"F2.opPattern","COPY",FACE,{"derivedFrom":subQ0,"instanceName":"6"}),makeQuery(id+"F2.opPattern","COPY",FACE,{"derivedFrom":subQ0,"instanceName":"7"}),makeQuery(id+"F2.opPattern","COPY",FACE,{"derivedFrom":subQ0,"instanceName":"8"}),makeQuery(id+"F2.opPattern","COPY",FACE,{"derivedFrom":subQ0,"instanceName":"9"}),makeQuery(id+"F2.opPattern","COPY",FACE,{"derivedFrom":subQ0,"instanceName":"10"}),makeQuery(id+"F2.opPattern","COPY",FACE,{"derivedFrom":subQ0,"instanceName":"11"}),makeQuery(id+"F2.opPattern","COPY",FACE,{"derivedFrom":subQ0,"instanceName":"12"}),makeQuery(id+"F2.opPattern","COPY",FACE,{"derivedFrom":subQ0,"instanceName":"13"}),makeQuery(id+"F2.opPattern","COPY",FACE,{"derivedFrom":subQ0,"instanceName":"16"})]});}
            var Q42;
            {var subQ0=makeQuery(id+"F1.opExtrude","SWEPT_FACE",FACE,{"disambiguationData":[OSD([sQuery(id+"F0.wireOp",EDGE,"E0")])]});Q42=makeQuery(id+"F3.opBoolean","INTERSECT",EDGE,{"disambiguationData":[topologyDisambiguationEdgeConnected([makeQuery(id+"F2.opPattern","COPY",FACE,{"derivedFrom":makeQuery(id+"F1.opExtrude","SWEPT_FACE",FACE,{"disambiguationData":[OSD([sQuery(id+"F0.wireOp",EDGE,"E12.MirrorCS")])]}),"instanceName":"15"})])],"derivedFrom":[subQ0,makeQuery(id+"F2.opPattern","COPY",FACE,{"derivedFrom":subQ0,"instanceName":"1"}),makeQuery(id+"F2.opPattern","COPY",FACE,{"derivedFrom":subQ0,"instanceName":"2"}),makeQuery(id+"F2.opPattern","COPY",FACE,{"derivedFrom":subQ0,"instanceName":"3"}),makeQuery(id+"F2.opPattern","COPY",FACE,{"derivedFrom":subQ0,"instanceName":"4"}),makeQuery(id+"F2.opPattern","COPY",FACE,{"derivedFrom":subQ0,"instanceName":"5"}),makeQuery(id+"F2.opPattern","COPY",FACE,{"derivedFrom":subQ0,"instanceName":"6"}),makeQuery(id+"F2.opPattern","COPY",FACE,{"derivedFrom":subQ0,"instanceName":"7"}),makeQuery(id+"F2.opPattern","COPY",FACE,{"derivedFrom":subQ0,"instanceName":"8"}),makeQuery(id+"F2.opPattern","COPY",FACE,{"derivedFrom":subQ0,"instanceName":"9"}),makeQuery(id+"F2.opPattern","COPY",FACE,{"derivedFrom":subQ0,"instanceName":"10"}),makeQuery(id+"F2.opPattern","COPY",FACE,{"derivedFrom":subQ0,"instanceName":"11"}),makeQuery(id+"F2.opPattern","COPY",FACE,{"derivedFrom":subQ0,"instanceName":"12"}),makeQuery(id+"F2.opPattern","COPY",FACE,{"derivedFrom":subQ0,"instanceName":"13"}),makeQuery(id+"F2.opPattern","COPY",FACE,{"derivedFrom":subQ0,"instanceName":"14"}),makeQuery(id+"F2.opPattern","COPY",FACE,{"derivedFrom":subQ0,"instanceName":"16"}),makeQuery(id+"F2.opPattern","COPY",FACE,{"derivedFrom":subQ0,"instanceName":"17"}),makeQuery(id+"F2.opPattern","COPY",FACE,{"derivedFrom":subQ0,"instanceName":"18"})]});}
            var Q43;
            {var subQ0=makeQuery(id+"F1.opExtrude","SWEPT_FACE",FACE,{"disambiguationData":[OSD([sQuery(id+"F0.wireOp",EDGE,"E0")])]});Q43=makeQuery(id+"F3.opBoolean","INTERSECT",EDGE,{"disambiguationData":[topologyDisambiguationEdgeConnected([makeQuery(id+"F2.opPattern","COPY",FACE,{"derivedFrom":makeQuery(id+"F1.opExtrude","SWEPT_FACE",FACE,{"disambiguationData":[OSD([sQuery(id+"F0.wireOp",EDGE,"E11")])]}),"instanceName":"11"})])],"derivedFrom":[subQ0,makeQuery(id+"F2.opPattern","COPY",FACE,{"derivedFrom":subQ0,"instanceName":"1"}),makeQuery(id+"F2.opPattern","COPY",FACE,{"derivedFrom":subQ0,"instanceName":"2"}),makeQuery(id+"F2.opPattern","COPY",FACE,{"derivedFrom":subQ0,"instanceName":"3"}),makeQuery(id+"F2.opPattern","COPY",FACE,{"derivedFrom":subQ0,"instanceName":"4"}),makeQuery(id+"F2.opPattern","COPY",FACE,{"derivedFrom":subQ0,"instanceName":"5"}),makeQuery(id+"F2.opPattern","COPY",FACE,{"derivedFrom":subQ0,"instanceName":"6"}),makeQuery(id+"F2.opPattern","COPY",FACE,{"derivedFrom":subQ0,"instanceName":"7"}),makeQuery(id+"F2.opPattern","COPY",FACE,{"derivedFrom":subQ0,"instanceName":"8"}),makeQuery(id+"F2.opPattern","COPY",FACE,{"derivedFrom":subQ0,"instanceName":"9"}),makeQuery(id+"F2.opPattern","COPY",FACE,{"derivedFrom":subQ0,"instanceName":"10"}),makeQuery(id+"F2.opPattern","COPY",FACE,{"derivedFrom":subQ0,"instanceName":"12"})]});}
            var Q44;
            {var subQ0=makeQuery(id+"F1.opExtrude","SWEPT_FACE",FACE,{"disambiguationData":[OSD([sQuery(id+"F0.wireOp",EDGE,"E0")])]});Q44=makeQuery(id+"F3.opBoolean","INTERSECT",EDGE,{"disambiguationData":[topologyDisambiguationEdgeConnected([makeQuery(id+"F2.opPattern","COPY",FACE,{"derivedFrom":makeQuery(id+"F1.opExtrude","SWEPT_FACE",FACE,{"disambiguationData":[OSD([sQuery(id+"F0.wireOp",EDGE,"E11")])]}),"instanceName":"12"})])],"derivedFrom":[subQ0,makeQuery(id+"F2.opPattern","COPY",FACE,{"derivedFrom":subQ0,"instanceName":"1"}),makeQuery(id+"F2.opPattern","COPY",FACE,{"derivedFrom":subQ0,"instanceName":"2"}),makeQuery(id+"F2.opPattern","COPY",FACE,{"derivedFrom":subQ0,"instanceName":"3"}),makeQuery(id+"F2.opPattern","COPY",FACE,{"derivedFrom":subQ0,"instanceName":"4"}),makeQuery(id+"F2.opPattern","COPY",FACE,{"derivedFrom":subQ0,"instanceName":"5"}),makeQuery(id+"F2.opPattern","COPY",FACE,{"derivedFrom":subQ0,"instanceName":"6"}),makeQuery(id+"F2.opPattern","COPY",FACE,{"derivedFrom":subQ0,"instanceName":"7"}),makeQuery(id+"F2.opPattern","COPY",FACE,{"derivedFrom":subQ0,"instanceName":"8"}),makeQuery(id+"F2.opPattern","COPY",FACE,{"derivedFrom":subQ0,"instanceName":"9"}),makeQuery(id+"F2.opPattern","COPY",FACE,{"derivedFrom":subQ0,"instanceName":"10"}),makeQuery(id+"F2.opPattern","COPY",FACE,{"derivedFrom":subQ0,"instanceName":"11"}),makeQuery(id+"F2.opPattern","COPY",FACE,{"derivedFrom":subQ0,"instanceName":"13"})]});}
            var Q45;
            {var subQ0=makeQuery(id+"F1.opExtrude","SWEPT_FACE",FACE,{"disambiguationData":[OSD([sQuery(id+"F0.wireOp",EDGE,"E0")])]});Q45=makeQuery(id+"F3.opBoolean","INTERSECT",EDGE,{"disambiguationData":[topologyDisambiguationEdgeConnected([makeQuery(id+"F2.opPattern","COPY",FACE,{"derivedFrom":makeQuery(id+"F1.opExtrude","SWEPT_FACE",FACE,{"disambiguationData":[OSD([sQuery(id+"F0.wireOp",EDGE,"E11")])]}),"instanceName":"13"})])],"derivedFrom":[subQ0,makeQuery(id+"F2.opPattern","COPY",FACE,{"derivedFrom":subQ0,"instanceName":"1"}),makeQuery(id+"F2.opPattern","COPY",FACE,{"derivedFrom":subQ0,"instanceName":"2"}),makeQuery(id+"F2.opPattern","COPY",FACE,{"derivedFrom":subQ0,"instanceName":"3"}),makeQuery(id+"F2.opPattern","COPY",FACE,{"derivedFrom":subQ0,"instanceName":"4"}),makeQuery(id+"F2.opPattern","COPY",FACE,{"derivedFrom":subQ0,"instanceName":"5"}),makeQuery(id+"F2.opPattern","COPY",FACE,{"derivedFrom":subQ0,"instanceName":"6"}),makeQuery(id+"F2.opPattern","COPY",FACE,{"derivedFrom":subQ0,"instanceName":"7"}),makeQuery(id+"F2.opPattern","COPY",FACE,{"derivedFrom":subQ0,"instanceName":"8"}),makeQuery(id+"F2.opPattern","COPY",FACE,{"derivedFrom":subQ0,"instanceName":"9"}),makeQuery(id+"F2.opPattern","COPY",FACE,{"derivedFrom":subQ0,"instanceName":"10"}),makeQuery(id+"F2.opPattern","COPY",FACE,{"derivedFrom":subQ0,"instanceName":"11"}),makeQuery(id+"F2.opPattern","COPY",FACE,{"derivedFrom":subQ0,"instanceName":"12"}),makeQuery(id+"F2.opPattern","COPY",FACE,{"derivedFrom":subQ0,"instanceName":"14"})]});}
            var Q46;
            {var subQ0=makeQuery(id+"F1.opExtrude","SWEPT_FACE",FACE,{"disambiguationData":[OSD([sQuery(id+"F0.wireOp",EDGE,"E0")])]});Q46=makeQuery(id+"F3.opBoolean","INTERSECT",EDGE,{"disambiguationData":[topologyDisambiguationEdgeConnected([makeQuery(id+"F2.opPattern","COPY",FACE,{"derivedFrom":makeQuery(id+"F1.opExtrude","SWEPT_FACE",FACE,{"disambiguationData":[OSD([sQuery(id+"F0.wireOp",EDGE,"E11")])]}),"instanceName":"14"})])],"derivedFrom":[subQ0,makeQuery(id+"F2.opPattern","COPY",FACE,{"derivedFrom":subQ0,"instanceName":"1"}),makeQuery(id+"F2.opPattern","COPY",FACE,{"derivedFrom":subQ0,"instanceName":"2"}),makeQuery(id+"F2.opPattern","COPY",FACE,{"derivedFrom":subQ0,"instanceName":"3"}),makeQuery(id+"F2.opPattern","COPY",FACE,{"derivedFrom":subQ0,"instanceName":"4"}),makeQuery(id+"F2.opPattern","COPY",FACE,{"derivedFrom":subQ0,"instanceName":"5"}),makeQuery(id+"F2.opPattern","COPY",FACE,{"derivedFrom":subQ0,"instanceName":"6"}),makeQuery(id+"F2.opPattern","COPY",FACE,{"derivedFrom":subQ0,"instanceName":"7"}),makeQuery(id+"F2.opPattern","COPY",FACE,{"derivedFrom":subQ0,"instanceName":"8"}),makeQuery(id+"F2.opPattern","COPY",FACE,{"derivedFrom":subQ0,"instanceName":"9"}),makeQuery(id+"F2.opPattern","COPY",FACE,{"derivedFrom":subQ0,"instanceName":"10"}),makeQuery(id+"F2.opPattern","COPY",FACE,{"derivedFrom":subQ0,"instanceName":"11"}),makeQuery(id+"F2.opPattern","COPY",FACE,{"derivedFrom":subQ0,"instanceName":"12"}),makeQuery(id+"F2.opPattern","COPY",FACE,{"derivedFrom":subQ0,"instanceName":"13"}),makeQuery(id+"F2.opPattern","COPY",FACE,{"derivedFrom":subQ0,"instanceName":"16"})]});}
            var Q47;
            {var subQ0=makeQuery(id+"F1.opExtrude","SWEPT_FACE",FACE,{"disambiguationData":[OSD([sQuery(id+"F0.wireOp",EDGE,"E0")])]});Q47=makeQuery(id+"F3.opBoolean","INTERSECT",EDGE,{"disambiguationData":[topologyDisambiguationEdgeConnected([makeQuery(id+"F2.opPattern","COPY",FACE,{"derivedFrom":makeQuery(id+"F1.opExtrude","SWEPT_FACE",FACE,{"disambiguationData":[OSD([sQuery(id+"F0.wireOp",EDGE,"E11")])]}),"instanceName":"15"})])],"derivedFrom":[subQ0,makeQuery(id+"F2.opPattern","COPY",FACE,{"derivedFrom":subQ0,"instanceName":"1"}),makeQuery(id+"F2.opPattern","COPY",FACE,{"derivedFrom":subQ0,"instanceName":"2"}),makeQuery(id+"F2.opPattern","COPY",FACE,{"derivedFrom":subQ0,"instanceName":"3"}),makeQuery(id+"F2.opPattern","COPY",FACE,{"derivedFrom":subQ0,"instanceName":"4"}),makeQuery(id+"F2.opPattern","COPY",FACE,{"derivedFrom":subQ0,"instanceName":"5"}),makeQuery(id+"F2.opPattern","COPY",FACE,{"derivedFrom":subQ0,"instanceName":"6"}),makeQuery(id+"F2.opPattern","COPY",FACE,{"derivedFrom":subQ0,"instanceName":"7"}),makeQuery(id+"F2.opPattern","COPY",FACE,{"derivedFrom":subQ0,"instanceName":"8"}),makeQuery(id+"F2.opPattern","COPY",FACE,{"derivedFrom":subQ0,"instanceName":"9"}),makeQuery(id+"F2.opPattern","COPY",FACE,{"derivedFrom":subQ0,"instanceName":"10"}),makeQuery(id+"F2.opPattern","COPY",FACE,{"derivedFrom":subQ0,"instanceName":"11"}),makeQuery(id+"F2.opPattern","COPY",FACE,{"derivedFrom":subQ0,"instanceName":"12"}),makeQuery(id+"F2.opPattern","COPY",FACE,{"derivedFrom":subQ0,"instanceName":"13"}),makeQuery(id+"F2.opPattern","COPY",FACE,{"derivedFrom":subQ0,"instanceName":"14"}),makeQuery(id+"F2.opPattern","COPY",FACE,{"derivedFrom":subQ0,"instanceName":"16"}),makeQuery(id+"F2.opPattern","COPY",FACE,{"derivedFrom":subQ0,"instanceName":"17"}),makeQuery(id+"F2.opPattern","COPY",FACE,{"derivedFrom":subQ0,"instanceName":"18"})]});}
            var Q48;
            {var subQ0=makeQuery(id+"F1.opExtrude","SWEPT_FACE",FACE,{"disambiguationData":[OSD([sQuery(id+"F0.wireOp",EDGE,"E0")])]});Q48=makeQuery(id+"F3.opBoolean","INTERSECT",EDGE,{"disambiguationData":[topologyDisambiguationEdgeConnected([makeQuery(id+"F2.opPattern","COPY",FACE,{"derivedFrom":makeQuery(id+"F1.opExtrude","SWEPT_FACE",FACE,{"disambiguationData":[OSD([sQuery(id+"F0.wireOp",EDGE,"E11")])]}),"instanceName":"16"})])],"derivedFrom":[subQ0,makeQuery(id+"F2.opPattern","COPY",FACE,{"derivedFrom":subQ0,"instanceName":"1"}),makeQuery(id+"F2.opPattern","COPY",FACE,{"derivedFrom":subQ0,"instanceName":"2"}),makeQuery(id+"F2.opPattern","COPY",FACE,{"derivedFrom":subQ0,"instanceName":"3"}),makeQuery(id+"F2.opPattern","COPY",FACE,{"derivedFrom":subQ0,"instanceName":"4"}),makeQuery(id+"F2.opPattern","COPY",FACE,{"derivedFrom":subQ0,"instanceName":"5"}),makeQuery(id+"F2.opPattern","COPY",FACE,{"derivedFrom":subQ0,"instanceName":"6"}),makeQuery(id+"F2.opPattern","COPY",FACE,{"derivedFrom":subQ0,"instanceName":"7"}),makeQuery(id+"F2.opPattern","COPY",FACE,{"derivedFrom":subQ0,"instanceName":"8"}),makeQuery(id+"F2.opPattern","COPY",FACE,{"derivedFrom":subQ0,"instanceName":"9"}),makeQuery(id+"F2.opPattern","COPY",FACE,{"derivedFrom":subQ0,"instanceName":"10"}),makeQuery(id+"F2.opPattern","COPY",FACE,{"derivedFrom":subQ0,"instanceName":"11"}),makeQuery(id+"F2.opPattern","COPY",FACE,{"derivedFrom":subQ0,"instanceName":"12"}),makeQuery(id+"F2.opPattern","COPY",FACE,{"derivedFrom":subQ0,"instanceName":"13"}),makeQuery(id+"F2.opPattern","COPY",FACE,{"derivedFrom":subQ0,"instanceName":"14"}),makeQuery(id+"F2.opPattern","COPY",FACE,{"derivedFrom":subQ0,"instanceName":"17"})]});}
            var Q49;
            {var subQ0=makeQuery(id+"F1.opExtrude","SWEPT_FACE",FACE,{"disambiguationData":[OSD([sQuery(id+"F0.wireOp",EDGE,"E0")])]});Q49=makeQuery(id+"F3.opBoolean","INTERSECT",EDGE,{"disambiguationData":[topologyDisambiguationEdgeConnected([makeQuery(id+"F2.opPattern","COPY",FACE,{"derivedFrom":makeQuery(id+"F1.opExtrude","SWEPT_FACE",FACE,{"disambiguationData":[OSD([sQuery(id+"F0.wireOp",EDGE,"E12.MirrorCS")])]}),"instanceName":"16"})])],"derivedFrom":[subQ0,makeQuery(id+"F2.opPattern","COPY",FACE,{"derivedFrom":subQ0,"instanceName":"1"}),makeQuery(id+"F2.opPattern","COPY",FACE,{"derivedFrom":subQ0,"instanceName":"2"}),makeQuery(id+"F2.opPattern","COPY",FACE,{"derivedFrom":subQ0,"instanceName":"3"}),makeQuery(id+"F2.opPattern","COPY",FACE,{"derivedFrom":subQ0,"instanceName":"4"}),makeQuery(id+"F2.opPattern","COPY",FACE,{"derivedFrom":subQ0,"instanceName":"5"}),makeQuery(id+"F2.opPattern","COPY",FACE,{"derivedFrom":subQ0,"instanceName":"6"}),makeQuery(id+"F2.opPattern","COPY",FACE,{"derivedFrom":subQ0,"instanceName":"7"}),makeQuery(id+"F2.opPattern","COPY",FACE,{"derivedFrom":subQ0,"instanceName":"8"}),makeQuery(id+"F2.opPattern","COPY",FACE,{"derivedFrom":subQ0,"instanceName":"9"}),makeQuery(id+"F2.opPattern","COPY",FACE,{"derivedFrom":subQ0,"instanceName":"10"}),makeQuery(id+"F2.opPattern","COPY",FACE,{"derivedFrom":subQ0,"instanceName":"11"}),makeQuery(id+"F2.opPattern","COPY",FACE,{"derivedFrom":subQ0,"instanceName":"12"}),makeQuery(id+"F2.opPattern","COPY",FACE,{"derivedFrom":subQ0,"instanceName":"13"}),makeQuery(id+"F2.opPattern","COPY",FACE,{"derivedFrom":subQ0,"instanceName":"14"}),makeQuery(id+"F2.opPattern","COPY",FACE,{"derivedFrom":subQ0,"instanceName":"17"})]});}
            var Q50;
            {var subQ0=makeQuery(id+"F1.opExtrude","SWEPT_FACE",FACE,{"disambiguationData":[OSD([sQuery(id+"F0.wireOp",EDGE,"E0")])]});Q50=makeQuery(id+"F3.opBoolean","INTERSECT",EDGE,{"disambiguationData":[topologyDisambiguationEdgeConnected([makeQuery(id+"F2.opPattern","COPY",FACE,{"derivedFrom":makeQuery(id+"F1.opExtrude","SWEPT_FACE",FACE,{"disambiguationData":[OSD([sQuery(id+"F0.wireOp",EDGE,"E12.MirrorCS")])]}),"instanceName":"17"})])],"derivedFrom":[subQ0,makeQuery(id+"F2.opPattern","COPY",FACE,{"derivedFrom":subQ0,"instanceName":"1"}),makeQuery(id+"F2.opPattern","COPY",FACE,{"derivedFrom":subQ0,"instanceName":"2"}),makeQuery(id+"F2.opPattern","COPY",FACE,{"derivedFrom":subQ0,"instanceName":"3"}),makeQuery(id+"F2.opPattern","COPY",FACE,{"derivedFrom":subQ0,"instanceName":"4"}),makeQuery(id+"F2.opPattern","COPY",FACE,{"derivedFrom":subQ0,"instanceName":"5"}),makeQuery(id+"F2.opPattern","COPY",FACE,{"derivedFrom":subQ0,"instanceName":"6"}),makeQuery(id+"F2.opPattern","COPY",FACE,{"derivedFrom":subQ0,"instanceName":"7"}),makeQuery(id+"F2.opPattern","COPY",FACE,{"derivedFrom":subQ0,"instanceName":"8"}),makeQuery(id+"F2.opPattern","COPY",FACE,{"derivedFrom":subQ0,"instanceName":"9"}),makeQuery(id+"F2.opPattern","COPY",FACE,{"derivedFrom":subQ0,"instanceName":"10"}),makeQuery(id+"F2.opPattern","COPY",FACE,{"derivedFrom":subQ0,"instanceName":"11"}),makeQuery(id+"F2.opPattern","COPY",FACE,{"derivedFrom":subQ0,"instanceName":"12"}),makeQuery(id+"F2.opPattern","COPY",FACE,{"derivedFrom":subQ0,"instanceName":"13"}),makeQuery(id+"F2.opPattern","COPY",FACE,{"derivedFrom":subQ0,"instanceName":"14"}),makeQuery(id+"F2.opPattern","COPY",FACE,{"derivedFrom":subQ0,"instanceName":"15"}),makeQuery(id+"F2.opPattern","COPY",FACE,{"derivedFrom":subQ0,"instanceName":"16"})]});}
            var Q51;
            {var subQ0=makeQuery(id+"F1.opExtrude","SWEPT_FACE",FACE,{"disambiguationData":[OSD([sQuery(id+"F0.wireOp",EDGE,"E0")])]});Q51=makeQuery(id+"F3.opBoolean","INTERSECT",EDGE,{"disambiguationData":[topologyDisambiguationEdgeConnected([makeQuery(id+"F2.opPattern","COPY",FACE,{"derivedFrom":makeQuery(id+"F1.opExtrude","SWEPT_FACE",FACE,{"disambiguationData":[OSD([sQuery(id+"F0.wireOp",EDGE,"E12.MirrorCS")])]}),"instanceName":"18"})])],"derivedFrom":[subQ0,makeQuery(id+"F2.opPattern","COPY",FACE,{"derivedFrom":subQ0,"instanceName":"1"}),makeQuery(id+"F2.opPattern","COPY",FACE,{"derivedFrom":subQ0,"instanceName":"2"}),makeQuery(id+"F2.opPattern","COPY",FACE,{"derivedFrom":subQ0,"instanceName":"3"}),makeQuery(id+"F2.opPattern","COPY",FACE,{"derivedFrom":subQ0,"instanceName":"4"}),makeQuery(id+"F2.opPattern","COPY",FACE,{"derivedFrom":subQ0,"instanceName":"5"}),makeQuery(id+"F2.opPattern","COPY",FACE,{"derivedFrom":subQ0,"instanceName":"6"}),makeQuery(id+"F2.opPattern","COPY",FACE,{"derivedFrom":subQ0,"instanceName":"7"}),makeQuery(id+"F2.opPattern","COPY",FACE,{"derivedFrom":subQ0,"instanceName":"8"}),makeQuery(id+"F2.opPattern","COPY",FACE,{"derivedFrom":subQ0,"instanceName":"9"}),makeQuery(id+"F2.opPattern","COPY",FACE,{"derivedFrom":subQ0,"instanceName":"10"}),makeQuery(id+"F2.opPattern","COPY",FACE,{"derivedFrom":subQ0,"instanceName":"11"}),makeQuery(id+"F2.opPattern","COPY",FACE,{"derivedFrom":subQ0,"instanceName":"12"}),makeQuery(id+"F2.opPattern","COPY",FACE,{"derivedFrom":subQ0,"instanceName":"13"}),makeQuery(id+"F2.opPattern","COPY",FACE,{"derivedFrom":subQ0,"instanceName":"14"}),makeQuery(id+"F2.opPattern","COPY",FACE,{"derivedFrom":subQ0,"instanceName":"15"}),makeQuery(id+"F2.opPattern","COPY",FACE,{"derivedFrom":subQ0,"instanceName":"16"}),makeQuery(id+"F2.opPattern","COPY",FACE,{"derivedFrom":subQ0,"instanceName":"17"}),makeQuery(id+"F2.opPattern","COPY",FACE,{"derivedFrom":subQ0,"instanceName":"19"})]});}
            var Q52;
            {var subQ0=makeQuery(id+"F1.opExtrude","SWEPT_FACE",FACE,{"disambiguationData":[OSD([sQuery(id+"F0.wireOp",EDGE,"E0")])]});Q52=makeQuery(id+"F3.opBoolean","INTERSECT",EDGE,{"disambiguationData":[topologyDisambiguationEdgeConnected([makeQuery(id+"F2.opPattern","COPY",FACE,{"derivedFrom":makeQuery(id+"F1.opExtrude","SWEPT_FACE",FACE,{"disambiguationData":[OSD([sQuery(id+"F0.wireOp",EDGE,"E12.MirrorCS")])]}),"instanceName":"19"})])],"derivedFrom":[subQ0,makeQuery(id+"F2.opPattern","COPY",FACE,{"derivedFrom":subQ0,"instanceName":"1"}),makeQuery(id+"F2.opPattern","COPY",FACE,{"derivedFrom":subQ0,"instanceName":"2"}),makeQuery(id+"F2.opPattern","COPY",FACE,{"derivedFrom":subQ0,"instanceName":"3"}),makeQuery(id+"F2.opPattern","COPY",FACE,{"derivedFrom":subQ0,"instanceName":"4"}),makeQuery(id+"F2.opPattern","COPY",FACE,{"derivedFrom":subQ0,"instanceName":"5"}),makeQuery(id+"F2.opPattern","COPY",FACE,{"derivedFrom":subQ0,"instanceName":"6"}),makeQuery(id+"F2.opPattern","COPY",FACE,{"derivedFrom":subQ0,"instanceName":"7"}),makeQuery(id+"F2.opPattern","COPY",FACE,{"derivedFrom":subQ0,"instanceName":"8"}),makeQuery(id+"F2.opPattern","COPY",FACE,{"derivedFrom":subQ0,"instanceName":"9"}),makeQuery(id+"F2.opPattern","COPY",FACE,{"derivedFrom":subQ0,"instanceName":"10"}),makeQuery(id+"F2.opPattern","COPY",FACE,{"derivedFrom":subQ0,"instanceName":"11"}),makeQuery(id+"F2.opPattern","COPY",FACE,{"derivedFrom":subQ0,"instanceName":"12"}),makeQuery(id+"F2.opPattern","COPY",FACE,{"derivedFrom":subQ0,"instanceName":"13"}),makeQuery(id+"F2.opPattern","COPY",FACE,{"derivedFrom":subQ0,"instanceName":"14"}),makeQuery(id+"F2.opPattern","COPY",FACE,{"derivedFrom":subQ0,"instanceName":"15"}),makeQuery(id+"F2.opPattern","COPY",FACE,{"derivedFrom":subQ0,"instanceName":"16"}),makeQuery(id+"F2.opPattern","COPY",FACE,{"derivedFrom":subQ0,"instanceName":"17"}),makeQuery(id+"F2.opPattern","COPY",FACE,{"derivedFrom":subQ0,"instanceName":"18"}),makeQuery(id+"F2.opPattern","COPY",FACE,{"derivedFrom":subQ0,"instanceName":"20"})]});}
            var Q53;
            {var subQ0=makeQuery(id+"F1.opExtrude","SWEPT_FACE",FACE,{"disambiguationData":[OSD([sQuery(id+"F0.wireOp",EDGE,"E0")])]});Q53=makeQuery(id+"F3.opBoolean","INTERSECT",EDGE,{"disambiguationData":[topologyDisambiguationEdgeConnected([makeQuery(id+"F2.opPattern","COPY",FACE,{"derivedFrom":makeQuery(id+"F1.opExtrude","SWEPT_FACE",FACE,{"disambiguationData":[OSD([sQuery(id+"F0.wireOp",EDGE,"E11")])]}),"instanceName":"17"})])],"derivedFrom":[subQ0,makeQuery(id+"F2.opPattern","COPY",FACE,{"derivedFrom":subQ0,"instanceName":"1"}),makeQuery(id+"F2.opPattern","COPY",FACE,{"derivedFrom":subQ0,"instanceName":"2"}),makeQuery(id+"F2.opPattern","COPY",FACE,{"derivedFrom":subQ0,"instanceName":"3"}),makeQuery(id+"F2.opPattern","COPY",FACE,{"derivedFrom":subQ0,"instanceName":"4"}),makeQuery(id+"F2.opPattern","COPY",FACE,{"derivedFrom":subQ0,"instanceName":"5"}),makeQuery(id+"F2.opPattern","COPY",FACE,{"derivedFrom":subQ0,"instanceName":"6"}),makeQuery(id+"F2.opPattern","COPY",FACE,{"derivedFrom":subQ0,"instanceName":"7"}),makeQuery(id+"F2.opPattern","COPY",FACE,{"derivedFrom":subQ0,"instanceName":"8"}),makeQuery(id+"F2.opPattern","COPY",FACE,{"derivedFrom":subQ0,"instanceName":"9"}),makeQuery(id+"F2.opPattern","COPY",FACE,{"derivedFrom":subQ0,"instanceName":"10"}),makeQuery(id+"F2.opPattern","COPY",FACE,{"derivedFrom":subQ0,"instanceName":"11"}),makeQuery(id+"F2.opPattern","COPY",FACE,{"derivedFrom":subQ0,"instanceName":"12"}),makeQuery(id+"F2.opPattern","COPY",FACE,{"derivedFrom":subQ0,"instanceName":"13"}),makeQuery(id+"F2.opPattern","COPY",FACE,{"derivedFrom":subQ0,"instanceName":"14"}),makeQuery(id+"F2.opPattern","COPY",FACE,{"derivedFrom":subQ0,"instanceName":"15"}),makeQuery(id+"F2.opPattern","COPY",FACE,{"derivedFrom":subQ0,"instanceName":"16"})]});}
            var Q54;
            {var subQ0=makeQuery(id+"F1.opExtrude","SWEPT_FACE",FACE,{"disambiguationData":[OSD([sQuery(id+"F0.wireOp",EDGE,"E0")])]});Q54=makeQuery(id+"F3.opBoolean","INTERSECT",EDGE,{"disambiguationData":[topologyDisambiguationEdgeConnected([makeQuery(id+"F2.opPattern","COPY",FACE,{"derivedFrom":makeQuery(id+"F1.opExtrude","SWEPT_FACE",FACE,{"disambiguationData":[OSD([sQuery(id+"F0.wireOp",EDGE,"E11")])]}),"instanceName":"18"})])],"derivedFrom":[subQ0,makeQuery(id+"F2.opPattern","COPY",FACE,{"derivedFrom":subQ0,"instanceName":"1"}),makeQuery(id+"F2.opPattern","COPY",FACE,{"derivedFrom":subQ0,"instanceName":"2"}),makeQuery(id+"F2.opPattern","COPY",FACE,{"derivedFrom":subQ0,"instanceName":"3"}),makeQuery(id+"F2.opPattern","COPY",FACE,{"derivedFrom":subQ0,"instanceName":"4"}),makeQuery(id+"F2.opPattern","COPY",FACE,{"derivedFrom":subQ0,"instanceName":"5"}),makeQuery(id+"F2.opPattern","COPY",FACE,{"derivedFrom":subQ0,"instanceName":"6"}),makeQuery(id+"F2.opPattern","COPY",FACE,{"derivedFrom":subQ0,"instanceName":"7"}),makeQuery(id+"F2.opPattern","COPY",FACE,{"derivedFrom":subQ0,"instanceName":"8"}),makeQuery(id+"F2.opPattern","COPY",FACE,{"derivedFrom":subQ0,"instanceName":"9"}),makeQuery(id+"F2.opPattern","COPY",FACE,{"derivedFrom":subQ0,"instanceName":"10"}),makeQuery(id+"F2.opPattern","COPY",FACE,{"derivedFrom":subQ0,"instanceName":"11"}),makeQuery(id+"F2.opPattern","COPY",FACE,{"derivedFrom":subQ0,"instanceName":"12"}),makeQuery(id+"F2.opPattern","COPY",FACE,{"derivedFrom":subQ0,"instanceName":"13"}),makeQuery(id+"F2.opPattern","COPY",FACE,{"derivedFrom":subQ0,"instanceName":"14"}),makeQuery(id+"F2.opPattern","COPY",FACE,{"derivedFrom":subQ0,"instanceName":"15"}),makeQuery(id+"F2.opPattern","COPY",FACE,{"derivedFrom":subQ0,"instanceName":"16"}),makeQuery(id+"F2.opPattern","COPY",FACE,{"derivedFrom":subQ0,"instanceName":"17"}),makeQuery(id+"F2.opPattern","COPY",FACE,{"derivedFrom":subQ0,"instanceName":"19"})]});}
            var Q55;
            {var subQ0=makeQuery(id+"F1.opExtrude","SWEPT_FACE",FACE,{"disambiguationData":[OSD([sQuery(id+"F0.wireOp",EDGE,"E0")])]});Q55=makeQuery(id+"F3.opBoolean","INTERSECT",EDGE,{"disambiguationData":[topologyDisambiguationEdgeConnected([makeQuery(id+"F2.opPattern","COPY",FACE,{"derivedFrom":makeQuery(id+"F1.opExtrude","SWEPT_FACE",FACE,{"disambiguationData":[OSD([sQuery(id+"F0.wireOp",EDGE,"E11")])]}),"instanceName":"19"})])],"derivedFrom":[subQ0,makeQuery(id+"F2.opPattern","COPY",FACE,{"derivedFrom":subQ0,"instanceName":"1"}),makeQuery(id+"F2.opPattern","COPY",FACE,{"derivedFrom":subQ0,"instanceName":"2"}),makeQuery(id+"F2.opPattern","COPY",FACE,{"derivedFrom":subQ0,"instanceName":"3"}),makeQuery(id+"F2.opPattern","COPY",FACE,{"derivedFrom":subQ0,"instanceName":"4"}),makeQuery(id+"F2.opPattern","COPY",FACE,{"derivedFrom":subQ0,"instanceName":"5"}),makeQuery(id+"F2.opPattern","COPY",FACE,{"derivedFrom":subQ0,"instanceName":"6"}),makeQuery(id+"F2.opPattern","COPY",FACE,{"derivedFrom":subQ0,"instanceName":"7"}),makeQuery(id+"F2.opPattern","COPY",FACE,{"derivedFrom":subQ0,"instanceName":"8"}),makeQuery(id+"F2.opPattern","COPY",FACE,{"derivedFrom":subQ0,"instanceName":"9"}),makeQuery(id+"F2.opPattern","COPY",FACE,{"derivedFrom":subQ0,"instanceName":"10"}),makeQuery(id+"F2.opPattern","COPY",FACE,{"derivedFrom":subQ0,"instanceName":"11"}),makeQuery(id+"F2.opPattern","COPY",FACE,{"derivedFrom":subQ0,"instanceName":"12"}),makeQuery(id+"F2.opPattern","COPY",FACE,{"derivedFrom":subQ0,"instanceName":"13"}),makeQuery(id+"F2.opPattern","COPY",FACE,{"derivedFrom":subQ0,"instanceName":"14"}),makeQuery(id+"F2.opPattern","COPY",FACE,{"derivedFrom":subQ0,"instanceName":"15"}),makeQuery(id+"F2.opPattern","COPY",FACE,{"derivedFrom":subQ0,"instanceName":"16"}),makeQuery(id+"F2.opPattern","COPY",FACE,{"derivedFrom":subQ0,"instanceName":"17"}),makeQuery(id+"F2.opPattern","COPY",FACE,{"derivedFrom":subQ0,"instanceName":"18"}),makeQuery(id+"F2.opPattern","COPY",FACE,{"derivedFrom":subQ0,"instanceName":"20"})]});}
            var Q56;
            {var subQ0=makeQuery(id+"F1.opExtrude","SWEPT_FACE",FACE,{"disambiguationData":[OSD([sQuery(id+"F0.wireOp",EDGE,"E0")])]});Q56=makeQuery(id+"F3.opBoolean","INTERSECT",EDGE,{"disambiguationData":[topologyDisambiguationEdgeConnected([makeQuery(id+"F2.opPattern","COPY",FACE,{"derivedFrom":makeQuery(id+"F1.opExtrude","SWEPT_FACE",FACE,{"disambiguationData":[OSD([sQuery(id+"F0.wireOp",EDGE,"E12.MirrorCS")])]}),"instanceName":"20"})])],"derivedFrom":[subQ0,makeQuery(id+"F2.opPattern","COPY",FACE,{"derivedFrom":subQ0,"instanceName":"1"}),makeQuery(id+"F2.opPattern","COPY",FACE,{"derivedFrom":subQ0,"instanceName":"2"}),makeQuery(id+"F2.opPattern","COPY",FACE,{"derivedFrom":subQ0,"instanceName":"3"}),makeQuery(id+"F2.opPattern","COPY",FACE,{"derivedFrom":subQ0,"instanceName":"4"}),makeQuery(id+"F2.opPattern","COPY",FACE,{"derivedFrom":subQ0,"instanceName":"5"}),makeQuery(id+"F2.opPattern","COPY",FACE,{"derivedFrom":subQ0,"instanceName":"6"}),makeQuery(id+"F2.opPattern","COPY",FACE,{"derivedFrom":subQ0,"instanceName":"7"}),makeQuery(id+"F2.opPattern","COPY",FACE,{"derivedFrom":subQ0,"instanceName":"8"}),makeQuery(id+"F2.opPattern","COPY",FACE,{"derivedFrom":subQ0,"instanceName":"9"}),makeQuery(id+"F2.opPattern","COPY",FACE,{"derivedFrom":subQ0,"instanceName":"10"}),makeQuery(id+"F2.opPattern","COPY",FACE,{"derivedFrom":subQ0,"instanceName":"11"}),makeQuery(id+"F2.opPattern","COPY",FACE,{"derivedFrom":subQ0,"instanceName":"12"}),makeQuery(id+"F2.opPattern","COPY",FACE,{"derivedFrom":subQ0,"instanceName":"13"}),makeQuery(id+"F2.opPattern","COPY",FACE,{"derivedFrom":subQ0,"instanceName":"14"}),makeQuery(id+"F2.opPattern","COPY",FACE,{"derivedFrom":subQ0,"instanceName":"15"}),makeQuery(id+"F2.opPattern","COPY",FACE,{"derivedFrom":subQ0,"instanceName":"16"}),makeQuery(id+"F2.opPattern","COPY",FACE,{"derivedFrom":subQ0,"instanceName":"17"}),makeQuery(id+"F2.opPattern","COPY",FACE,{"derivedFrom":subQ0,"instanceName":"18"}),makeQuery(id+"F2.opPattern","COPY",FACE,{"derivedFrom":subQ0,"instanceName":"19"}),makeQuery(id+"F2.opPattern","COPY",FACE,{"derivedFrom":subQ0,"instanceName":"21"})]});}
            var Q57;
            {var subQ0=makeQuery(id+"F1.opExtrude","SWEPT_FACE",FACE,{"disambiguationData":[OSD([sQuery(id+"F0.wireOp",EDGE,"E0")])]});Q57=makeQuery(id+"F3.opBoolean","INTERSECT",EDGE,{"disambiguationData":[topologyDisambiguationEdgeConnected([makeQuery(id+"F2.opPattern","COPY",FACE,{"derivedFrom":makeQuery(id+"F1.opExtrude","SWEPT_FACE",FACE,{"disambiguationData":[OSD([sQuery(id+"F0.wireOp",EDGE,"E12.MirrorCS")])]}),"instanceName":"21"})])],"derivedFrom":[subQ0,makeQuery(id+"F2.opPattern","COPY",FACE,{"derivedFrom":subQ0,"instanceName":"1"}),makeQuery(id+"F2.opPattern","COPY",FACE,{"derivedFrom":subQ0,"instanceName":"2"}),makeQuery(id+"F2.opPattern","COPY",FACE,{"derivedFrom":subQ0,"instanceName":"3"}),makeQuery(id+"F2.opPattern","COPY",FACE,{"derivedFrom":subQ0,"instanceName":"4"}),makeQuery(id+"F2.opPattern","COPY",FACE,{"derivedFrom":subQ0,"instanceName":"5"}),makeQuery(id+"F2.opPattern","COPY",FACE,{"derivedFrom":subQ0,"instanceName":"6"}),makeQuery(id+"F2.opPattern","COPY",FACE,{"derivedFrom":subQ0,"instanceName":"7"}),makeQuery(id+"F2.opPattern","COPY",FACE,{"derivedFrom":subQ0,"instanceName":"8"}),makeQuery(id+"F2.opPattern","COPY",FACE,{"derivedFrom":subQ0,"instanceName":"9"}),makeQuery(id+"F2.opPattern","COPY",FACE,{"derivedFrom":subQ0,"instanceName":"10"}),makeQuery(id+"F2.opPattern","COPY",FACE,{"derivedFrom":subQ0,"instanceName":"11"}),makeQuery(id+"F2.opPattern","COPY",FACE,{"derivedFrom":subQ0,"instanceName":"12"}),makeQuery(id+"F2.opPattern","COPY",FACE,{"derivedFrom":subQ0,"instanceName":"13"}),makeQuery(id+"F2.opPattern","COPY",FACE,{"derivedFrom":subQ0,"instanceName":"14"}),makeQuery(id+"F2.opPattern","COPY",FACE,{"derivedFrom":subQ0,"instanceName":"15"}),makeQuery(id+"F2.opPattern","COPY",FACE,{"derivedFrom":subQ0,"instanceName":"16"}),makeQuery(id+"F2.opPattern","COPY",FACE,{"derivedFrom":subQ0,"instanceName":"17"}),makeQuery(id+"F2.opPattern","COPY",FACE,{"derivedFrom":subQ0,"instanceName":"18"}),makeQuery(id+"F2.opPattern","COPY",FACE,{"derivedFrom":subQ0,"instanceName":"19"}),makeQuery(id+"F2.opPattern","COPY",FACE,{"derivedFrom":subQ0,"instanceName":"20"}),makeQuery(id+"F2.opPattern","COPY",FACE,{"derivedFrom":subQ0,"instanceName":"22"})]});}
            var Q58;
            {var subQ0=makeQuery(id+"F1.opExtrude","SWEPT_FACE",FACE,{"disambiguationData":[OSD([sQuery(id+"F0.wireOp",EDGE,"E0")])]});Q58=makeQuery(id+"F3.opBoolean","INTERSECT",EDGE,{"disambiguationData":[topologyDisambiguationEdgeConnected([makeQuery(id+"F2.opPattern","COPY",FACE,{"derivedFrom":makeQuery(id+"F1.opExtrude","SWEPT_FACE",FACE,{"disambiguationData":[OSD([sQuery(id+"F0.wireOp",EDGE,"E11")])]}),"instanceName":"20"})])],"derivedFrom":[subQ0,makeQuery(id+"F2.opPattern","COPY",FACE,{"derivedFrom":subQ0,"instanceName":"1"}),makeQuery(id+"F2.opPattern","COPY",FACE,{"derivedFrom":subQ0,"instanceName":"2"}),makeQuery(id+"F2.opPattern","COPY",FACE,{"derivedFrom":subQ0,"instanceName":"3"}),makeQuery(id+"F2.opPattern","COPY",FACE,{"derivedFrom":subQ0,"instanceName":"4"}),makeQuery(id+"F2.opPattern","COPY",FACE,{"derivedFrom":subQ0,"instanceName":"5"}),makeQuery(id+"F2.opPattern","COPY",FACE,{"derivedFrom":subQ0,"instanceName":"6"}),makeQuery(id+"F2.opPattern","COPY",FACE,{"derivedFrom":subQ0,"instanceName":"7"}),makeQuery(id+"F2.opPattern","COPY",FACE,{"derivedFrom":subQ0,"instanceName":"8"}),makeQuery(id+"F2.opPattern","COPY",FACE,{"derivedFrom":subQ0,"instanceName":"9"}),makeQuery(id+"F2.opPattern","COPY",FACE,{"derivedFrom":subQ0,"instanceName":"10"}),makeQuery(id+"F2.opPattern","COPY",FACE,{"derivedFrom":subQ0,"instanceName":"11"}),makeQuery(id+"F2.opPattern","COPY",FACE,{"derivedFrom":subQ0,"instanceName":"12"}),makeQuery(id+"F2.opPattern","COPY",FACE,{"derivedFrom":subQ0,"instanceName":"13"}),makeQuery(id+"F2.opPattern","COPY",FACE,{"derivedFrom":subQ0,"instanceName":"14"}),makeQuery(id+"F2.opPattern","COPY",FACE,{"derivedFrom":subQ0,"instanceName":"15"}),makeQuery(id+"F2.opPattern","COPY",FACE,{"derivedFrom":subQ0,"instanceName":"16"}),makeQuery(id+"F2.opPattern","COPY",FACE,{"derivedFrom":subQ0,"instanceName":"17"}),makeQuery(id+"F2.opPattern","COPY",FACE,{"derivedFrom":subQ0,"instanceName":"18"}),makeQuery(id+"F2.opPattern","COPY",FACE,{"derivedFrom":subQ0,"instanceName":"19"}),makeQuery(id+"F2.opPattern","COPY",FACE,{"derivedFrom":subQ0,"instanceName":"21"})]});}
            fillet(context, id + "F4", {"entities" : qUnion([Q0, Q1, Q2, Q3, Q4, Q5, Q6, Q7, Q8, Q9, Q10, Q11, Q12, Q13, Q14, Q15, Q16, Q17, Q18, Q19, Q20, Q21, Q22, Q23, Q24, Q25, Q26, Q27, Q28, Q29, Q30, Q31, Q32, Q33, Q34, Q35, Q36, Q37, Q38, Q39, Q40, Q41, Q42, Q43, Q44, Q45, Q46, Q47, Q48, Q49, Q50, Q51, Q52, Q53, Q54, Q55, Q56, Q57, Q58]), "radius" : 1.02 * mm, "tangentPropagation" : true, "allowEdgeOverflow" : false});
        }
    });
